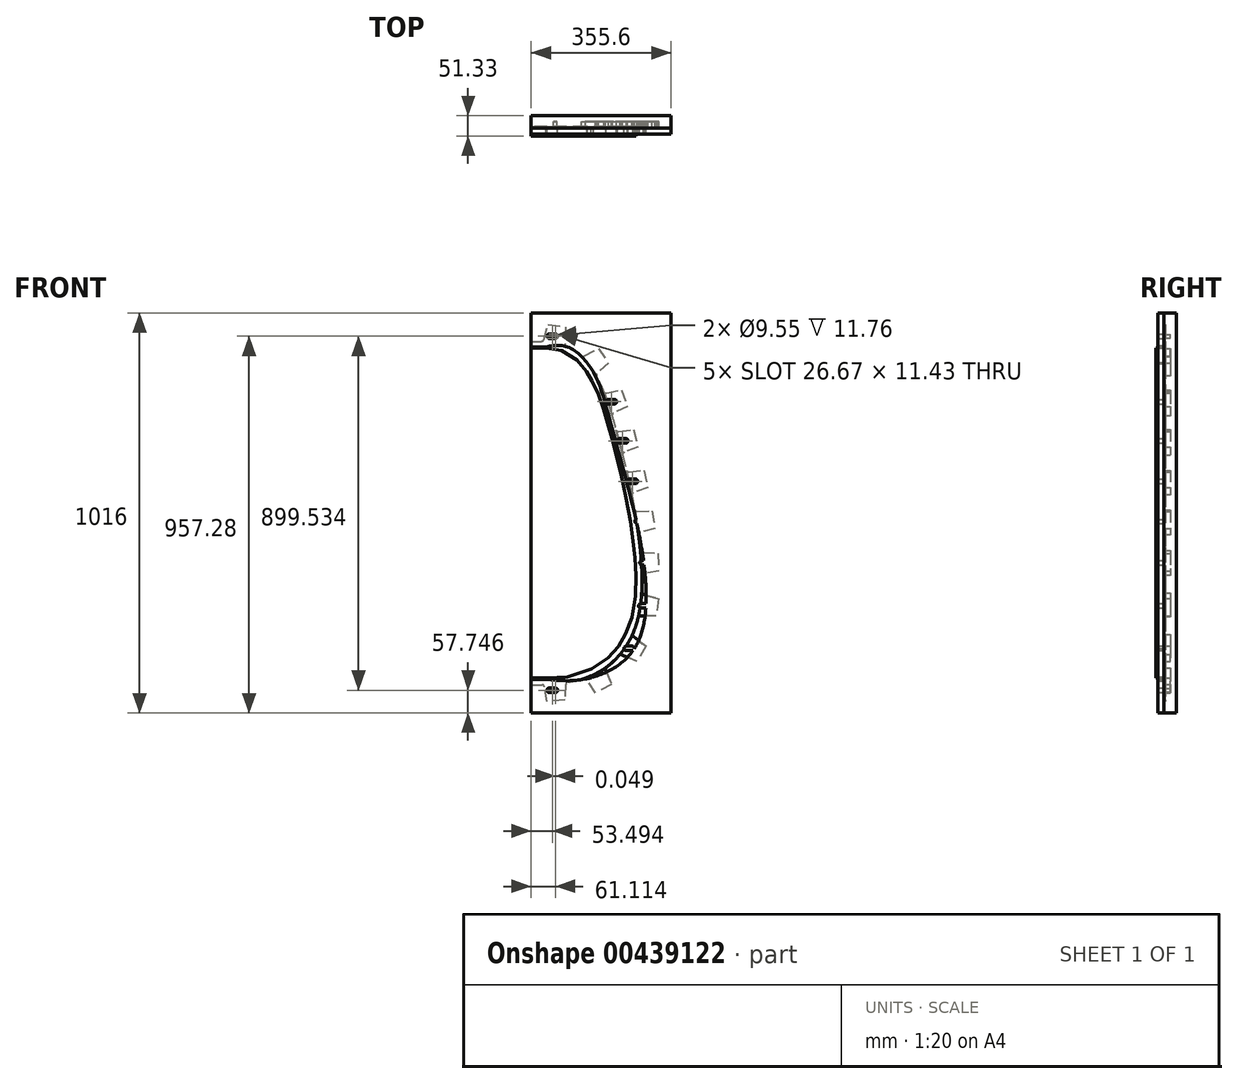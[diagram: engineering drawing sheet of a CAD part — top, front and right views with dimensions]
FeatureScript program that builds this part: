
annotation { "Feature Type Name" : "Feature", "Feature Type Description" : "" }
export const myFeature = defineFeature(function(context is Context, id is Id, definition is map)
    precondition{}
    {
        {
            var Q0;
            Q0=qCreatedBy(makeId("Front.planeOp"),FACE);
            var sketch = newSketch(context, id + "F0", { "sketchPlane" : qUnion([Q0])});
            skFitSpline(sketch, "E0", {"points": [v(-576.92, 670.47) * mm, v(-470.24, 606.97) * mm, v(-414.36, 467.27) * mm, v(-348.32, 137.07) * mm, v(-383.88, -82.64) * mm, v(-576.92, -174.08) * mm], "startDerivative": vector(1017.06, 0) * mm, "endDerivative": vector(-1410.71, 0) * mm});
            skLineSegment(sketch, "E1", {"start": v(-576.92, 670.47) * mm, "end": v(-576.92, -174.08) * mm, "construction": true});
            skFitSpline(sketch, "E2.MirrorCS", {"points": [v(-576.92, 670.47) * mm, v(-683.6, 606.97) * mm, v(-739.48, 467.27) * mm, v(-805.52, 137.07) * mm, v(-769.96, -82.64) * mm, v(-576.92, -174.08) * mm], "startDerivative": vector(-1017.06, 0) * mm, "endDerivative": vector(1410.71, 0) * mm});
            skSolve(sketch);
        }
        {
            var Q0;
            Q0=qCreatedBy(makeId("Front.planeOp"),FACE);
            var sketch = newSketch(context, id + "F1", { "sketchPlane" : qUnion([Q0])});
            skLineSegment(sketch, "E3.left", {"start": v(1043.34, 841.74) * mm, "end": v(1043.34, -174.26) * mm, "construction": true});
            skFitSpline(sketch, "E4", {"points": [v(1043.34, 756.01) * mm, v(1150.02, 692.51) * mm, v(1205.9, 552.81) * mm, v(1271.94, 222.61) * mm, v(1236.38, 2.9) * mm, v(1043.34, -88.54) * mm], "startDerivative": vector(1017.06, 0) * mm, "endDerivative": vector(-1775.42, 0) * mm});
            skFitSpline(sketch, "E5.0", {"points": [v(1043.34, 806.81) * mm, v(1050.54, 806.81) * mm, v(1064.65, 806) * mm, v(1084.8, 802.4) * mm, v(1103.69, 796.55) * mm, v(1121.1, 788.71) * mm, v(1136.85, 779.25) * mm, v(1150.91, 768.58) * mm, v(1161.28, 758.99) * mm, v(1168.83, 751.07) * mm, v(1174.15, 745.04) * mm, v(1179.14, 738.95) * mm, v(1183.83, 732.83) * mm, v(1187.5, 727.73) * mm, v(1190.31, 723.65) * mm, v(1192.36, 720.61) * mm, v(1194.35, 717.57) * mm, v(1196.96, 713.48) * mm, v(1200.11, 708.33) * mm, v(1203.75, 702.08) * mm, v(1208.4, 693.67) * mm, v(1213.85, 682.98) * mm, v(1219.89, 669.89) * mm, v(1225.5, 656.5) * mm, v(1232.5, 638.2) * mm, v(1238.98, 619.16) * mm, v(1244.47, 601.6) * mm, v(1247.59, 591.29) * mm, v(1249.93, 583.4) * mm, v(1251.9, 576.67) * mm, v(1253.47, 571.21) * mm, v(1254.66, 567.07) * mm, v(1255.86, 562.88) * mm, v(1257.48, 557.22) * mm, v(1259.52, 550) * mm, v(1262, 541.12) * mm, v(1265.36, 529) * mm, v(1269.6, 513.4) * mm, v(1274.72, 493.98) * mm, v(1281.54, 467.29) * mm, v(1289.92, 432.61) * mm, v(1299.39, 389.54) * mm, v(1307.88, 345.63) * mm, v(1313.83, 308.82) * mm, v(1317.72, 279.53) * mm, v(1320.15, 257.7) * mm, v(1321.73, 239.7) * mm, v(1322.7, 225.41) * mm, v(1323.45, 211.24) * mm, v(1324, 193.8) * mm, v(1324.03, 166.44) * mm, v(1322.49, 133.31) * mm, v(1318.05, 95.33) * mm, v(1312.15, 65.2) * mm, v(1306.08, 42.08) * mm, v(1301.7, 28.04) * mm, v(1297.85, 17.07) * mm, v(1294.78, 8.97) * mm, v(1291.54, 1) * mm, v(1288.68, -5.52) * mm, v(1286.3, -10.67) * mm, v(1284.48, -14.5) * mm, v(1282.6, -18.29) * mm, v(1280.69, -22.04) * mm, v(1278.7, -25.8) * mm, v(1275.96, -30.78) * mm, v(1272.35, -37) * mm, v(1267.69, -44.42) * mm, v(1260.99, -54.21) * mm, v(1251.62, -66.2) * mm, v(1238.62, -79.86) * mm, v(1223.79, -92.5) * mm, v(1207.15, -103.81) * mm, v(1188.83, -113.58) * mm, v(1168.9, -121.74) * mm, v(1147.4, -128.28) * mm, v(1124.3, -133.28) * mm, v(1099.43, -136.79) * mm, v(1072.64, -138.87) * mm, v(1053.37, -139.34) * mm, v(1043.34, -139.34) * mm]});
            skLineSegment(sketch, "E6", {"start": v(1043.34, 806.81) * mm, "end": v(1005.24, 806.81) * mm});
            skLineSegment(sketch, "E7", {"start": v(1005.24, 806.81) * mm, "end": v(1005.24, 756.01) * mm});
            skLineSegment(sketch, "E8", {"start": v(1005.24, 756.01) * mm, "end": v(1043.34, 756.01) * mm});
            skLineSegment(sketch, "E9", {"start": v(1043.34, -88.54) * mm, "end": v(1005.24, -88.54) * mm});
            skLineSegment(sketch, "E10", {"start": v(1005.24, -139.34) * mm, "end": v(1043.34, -139.34) * mm});
            skFitSpline(sketch, "E11.0", {"points": [v(1043.34, 784.67) * mm, v(1049.71, 784.67) * mm, v(1062.1, 783.95) * mm, v(1079.57, 780.82) * mm, v(1095.84, 775.78) * mm, v(1110.8, 769.04) * mm, v(1124.4, 760.88) * mm, v(1136.64, 751.6) * mm, v(1147.6, 741.46) * mm, v(1155.76, 732.53) * mm, v(1161.77, 725.2) * mm, v(1166.04, 719.62) * mm, v(1169.41, 714.95) * mm, v(1172, 711.19) * mm, v(1173.9, 708.37) * mm, v(1175.74, 705.55) * mm, v(1178.16, 701.75) * mm, v(1181.1, 696.97) * mm, v(1184.47, 691.16) * mm, v(1188.8, 683.32) * mm, v(1193.9, 673.32) * mm, v(1199.6, 660.98) * mm, v(1204.93, 648.27) * mm, v(1211.64, 630.76) * mm, v(1217.92, 612.3) * mm, v(1224.06, 592.64) * mm, v(1227.9, 579.8) * mm, v(1231.01, 569.16) * mm, v(1233.37, 560.99) * mm, v(1235.77, 552.6) * mm, v(1239.02, 541.12) * mm, v(1243.15, 526.26) * mm, v(1248.2, 507.67) * mm, v(1253.28, 488.41) * mm, v(1260.04, 461.96) * mm, v(1268.34, 427.62) * mm, v(1277.7, 385.05) * mm, v(1286.07, 341.74) * mm, v(1291.92, 305.55) * mm, v(1295.74, 276.84) * mm, v(1298.11, 255.5) * mm, v(1299.65, 237.95) * mm, v(1300.58, 224.07) * mm, v(1301.32, 210.33) * mm, v(1301.85, 193.43) * mm, v(1301.88, 166.98) * mm, v(1300.39, 135.07) * mm, v(1296.14, 98.7) * mm, v(1290.52, 70.05) * mm, v(1284.78, 48.18) * mm, v(1279.83, 32.3) * mm, v(1275.18, 19.55) * mm, v(1271.13, 9.62) * mm, v(1267.94, 2.32) * mm, v(1265.14, -3.64) * mm, v(1262.82, -8.34) * mm, v(1260.44, -12.98) * mm, v(1257.34, -18.74) * mm, v(1253.39, -25.56) * mm, v(1249.16, -32.28) * mm, v(1243.14, -41.07) * mm, v(1234.81, -51.72) * mm, v(1223.36, -63.75) * mm, v(1210.35, -74.85) * mm, v(1195.7, -84.8) * mm, v(1179.44, -93.48) * mm, v(1161.52, -100.82) * mm, v(1141.89, -106.8) * mm, v(1120.46, -111.44) * mm, v(1089.28, -115.85) * mm, v(1062.72, -117.19) * mm, v(1043.34, -117.19) * mm], "construction": true});
            skLineSegment(sketch, "E12", {"start": v(1043.34, -117.19) * mm, "end": v(1071.42, -116.5) * mm, "construction": true});
            skLineSegment(sketch, "E13", {"start": v(1071.42, -116.5) * mm, "end": v(1179.77, -92.97) * mm, "construction": true});
            skLineSegment(sketch, "E14", {"start": v(1179.77, -92.97) * mm, "end": v(1263.07, -7.82) * mm, "construction": true});
            skLineSegment(sketch, "E15", {"start": v(1263.07, -7.82) * mm, "end": v(1295.52, 97.75) * mm, "construction": true});
            skLineSegment(sketch, "E16", {"start": v(1295.52, 97.75) * mm, "end": v(1301.39, 207.04) * mm, "construction": true});
            skLineSegment(sketch, "E17", {"start": v(1301.39, 207.04) * mm, "end": v(1290.66, 312.82) * mm, "construction": true});
            skLineSegment(sketch, "E18", {"start": v(1290.66, 312.82) * mm, "end": v(1270.69, 416.63) * mm, "construction": true});
            skLineSegment(sketch, "E19", {"start": v(1270.69, 416.63) * mm, "end": v(1245.88, 516.18) * mm, "construction": true});
            skLineSegment(sketch, "E20", {"start": v(1245.88, 516.18) * mm, "end": v(1216.32, 616.8) * mm, "construction": true});
            skLineSegment(sketch, "E21", {"start": v(1216.32, 616.8) * mm, "end": v(1168.66, 715.98) * mm, "construction": true});
            skLineSegment(sketch, "E22", {"start": v(1168.66, 715.98) * mm, "end": v(1071.32, 782.2) * mm, "construction": true});
            skLineSegment(sketch, "E23", {"start": v(1071.32, 782.2) * mm, "end": v(1043.34, 784.67) * mm, "construction": true});
            skCircle(sketch, "E24", {"center": v(1071.42, -116.5) * mm, "radius": 4.76 * mm});
            skCircle(sketch, "E25", {"center": v(1179.77, -92.97) * mm, "radius": 4.76 * mm});
            skCircle(sketch, "E26", {"center": v(1263.07, -7.82) * mm, "radius": 4.76 * mm});
            skCircle(sketch, "E27", {"center": v(1295.52, 97.75) * mm, "radius": 4.76 * mm});
            skCircle(sketch, "E28", {"center": v(1301.39, 207.04) * mm, "radius": 4.76 * mm});
            skCircle(sketch, "E29", {"center": v(1290.66, 312.82) * mm, "radius": 4.76 * mm});
            skCircle(sketch, "E30", {"center": v(1270.69, 416.63) * mm, "radius": 4.76 * mm});
            skCircle(sketch, "E31", {"center": v(1245.88, 516.18) * mm, "radius": 4.76 * mm});
            skCircle(sketch, "E32", {"center": v(1216.32, 616.8) * mm, "radius": 4.76 * mm});
            skCircle(sketch, "E33", {"center": v(1168.66, 715.98) * mm, "radius": 4.76 * mm});
            skCircle(sketch, "E34", {"center": v(1071.32, 782.2) * mm, "radius": 4.76 * mm});
            skFitSpline(sketch, "E35.0", {"points": [v(1043.34, 752.4) * mm, v(1053.67, 752.4) * mm, v(1072.54, 750.1) * mm, v(1096.28, 740.96) * mm, v(1116.25, 727.3) * mm, v(1130.27, 713.02) * mm, v(1140.2, 700.45) * mm, v(1147.09, 690.59) * mm, v(1153.46, 680.47) * mm, v(1159.36, 670.04) * mm, v(1164.87, 659.25) * mm, v(1171.78, 644.27) * mm, v(1178.16, 628.3) * mm, v(1184.25, 611.1) * mm, v(1188.74, 597.54) * mm, v(1193.2, 583.23) * mm, v(1197.72, 568.14) * mm, v(1202.34, 552.2) * mm, v(1207.14, 535.36) * mm, v(1212.05, 517.7) * mm, v(1217.04, 499.33) * mm, v(1222.06, 480.3) * mm, v(1228.73, 454.2) * mm, v(1236.9, 420.35) * mm, v(1246.1, 378.5) * mm, v(1254.31, 336.06) * mm, v(1260.02, 300.77) * mm, v(1263.71, 272.91) * mm, v(1266.01, 252.3) * mm, v(1267.78, 232.03) * mm, v(1268.98, 212.22) * mm, v(1269.6, 192.89) * mm, v(1269.62, 167.77) * mm, v(1268.2, 137.64) * mm, v(1264.22, 103.61) * mm, v(1259.02, 77.1) * mm, v(1253.75, 57.06) * mm, v(1249.25, 42.62) * mm, v(1244.2, 28.78) * mm, v(1239.55, 17.76) * mm, v(1235.56, 9.26) * mm, v(1231.4, 0.97) * mm, v(1225.85, -8.98) * mm, v(1218.51, -20.19) * mm, v(1210.33, -30.64) * mm, v(1201.14, -40.3) * mm, v(1187.31, -52.07) * mm, v(1166.63, -64.67) * mm, v(1134.9, -76.05) * mm, v(1094.85, -83.24) * mm, v(1061.73, -84.93) * mm, v(1043.34, -84.93) * mm]});
            skLineSegment(sketch, "E36", {"start": v(1043.34, 752.4) * mm, "end": v(1005.24, 752.4) * mm});
            skLineSegment(sketch, "E37", {"start": v(1005.24, 756.01) * mm, "end": v(1005.24, 752.4) * mm});
            skLineSegment(sketch, "E38", {"start": v(1043.34, -117.19) * mm, "end": v(1005.24, -117.19) * mm});
            skLineSegment(sketch, "E39", {"start": v(1043.34, -84.93) * mm, "end": v(1005.24, -84.93) * mm});
            skLineSegment(sketch, "E40", {"start": v(1005.24, -139.34) * mm, "end": v(1005.24, -117.19) * mm});
            skLineSegment(sketch, "E41", {"start": v(1005.24, -88.54) * mm, "end": v(1005.24, -117.19) * mm});
            skLineSegment(sketch, "E42", {"start": v(1005.24, -88.54) * mm, "end": v(1005.24, -84.93) * mm});
            skLineSegment(sketch, "E43", {"start": v(1005.24, -84.93) * mm, "end": v(1005.24, 752.4) * mm});
            skFitSpline(sketch, "E44.0", {"points": [v(1043.34, 805.54) * mm, v(1050.5, 805.54) * mm, v(1064.5, 804.74) * mm, v(1084.5, 801.17) * mm, v(1103.24, 795.36) * mm, v(1120.5, 787.59) * mm, v(1136.14, 778.2) * mm, v(1150.1, 767.6) * mm, v(1160.4, 758.08) * mm, v(1167.9, 750.21) * mm, v(1173.18, 744.21) * mm, v(1178.15, 738.16) * mm, v(1182.8, 732.07) * mm, v(1186.47, 727) * mm, v(1189.26, 722.94) * mm, v(1191.3, 719.9) * mm, v(1193.28, 716.88) * mm, v(1195.88, 712.8) * mm, v(1199.02, 707.68) * mm, v(1202.64, 701.46) * mm, v(1207.27, 693.07) * mm, v(1212.7, 682.43) * mm, v(1218.72, 669.38) * mm, v(1224.32, 656.02) * mm, v(1231.31, 637.78) * mm, v(1237.78, 618.76) * mm, v(1243.25, 601.23) * mm, v(1246.37, 590.92) * mm, v(1248.71, 583.03) * mm, v(1250.67, 576.32) * mm, v(1252.25, 570.86) * mm, v(1253.44, 566.72) * mm, v(1254.64, 562.53) * mm, v(1256.26, 556.87) * mm, v(1258.3, 549.65) * mm, v(1260.78, 540.78) * mm, v(1264.13, 528.67) * mm, v(1268.37, 513.07) * mm, v(1273.49, 493.66) * mm, v(1280.3, 466.98) * mm, v(1288.68, 432.33) * mm, v(1298.14, 389.29) * mm, v(1306.63, 345.4) * mm, v(1312.57, 308.64) * mm, v(1316.46, 279.38) * mm, v(1318.89, 257.58) * mm, v(1320.46, 239.6) * mm, v(1321.43, 225.33) * mm, v(1322.18, 211.2) * mm, v(1322.73, 193.78) * mm, v(1322.76, 166.47) * mm, v(1321.22, 133.41) * mm, v(1316.8, 95.52) * mm, v(1310.91, 65.48) * mm, v(1304.85, 42.43) * mm, v(1300.5, 28.44) * mm, v(1296.66, 17.5) * mm, v(1293.6, 9.43) * mm, v(1290.37, 1.5) * mm, v(1287.52, -5) * mm, v(1285.16, -10.13) * mm, v(1283.34, -13.94) * mm, v(1281.47, -17.72) * mm, v(1279.56, -21.46) * mm, v(1277.58, -25.19) * mm, v(1274.86, -30.16) * mm, v(1271.27, -36.35) * mm, v(1266.63, -43.73) * mm, v(1259.96, -53.46) * mm, v(1250.66, -65.36) * mm, v(1237.75, -78.94) * mm, v(1223.02, -91.5) * mm, v(1206.5, -102.72) * mm, v(1188.29, -112.43) * mm, v(1168.48, -120.54) * mm, v(1147.09, -127.05) * mm, v(1124.07, -132.02) * mm, v(1099.3, -135.53) * mm, v(1072.58, -137.6) * mm, v(1053.35, -138.07) * mm, v(1043.34, -138.07) * mm], "construction": true});
            skFitSpline(sketch, "E45.0", {"points": [v(1043.34, 759.44) * mm, v(1054.2, 759.44) * mm, v(1074.2, 757) * mm, v(1099.6, 747.24) * mm, v(1120.84, 732.68) * mm, v(1135.55, 717.7) * mm, v(1145.87, 704.64) * mm, v(1152.96, 694.47) * mm, v(1159.5, 684.08) * mm, v(1167.58, 669.8) * mm, v(1176.64, 651.08) * mm, v(1184.75, 630.78) * mm, v(1190.9, 613.38) * mm, v(1195.44, 599.68) * mm, v(1199.94, 585.29) * mm, v(1204.47, 570.12) * mm, v(1209.1, 554.14) * mm, v(1213.9, 537.26) * mm, v(1218.83, 519.57) * mm, v(1223.84, 501.15) * mm, v(1228.87, 482.07) * mm, v(1235.56, 455.89) * mm, v(1243.77, 421.94) * mm, v(1253, 379.93) * mm, v(1261.24, 337.3) * mm, v(1266.97, 301.81) * mm, v(1270.7, 273.77) * mm, v(1273.01, 253) * mm, v(1274.8, 232.56) * mm, v(1276.01, 212.54) * mm, v(1276.63, 193) * mm, v(1276.66, 167.6) * mm, v(1275.23, 137.08) * mm, v(1271.18, 102.54) * mm, v(1265.9, 75.57) * mm, v(1260.52, 55.12) * mm, v(1255.92, 40.37) * mm, v(1250.76, 26.2) * mm, v(1245.99, 14.91) * mm, v(1241.89, 6.19) * mm, v(1237.6, -2.33) * mm, v(1231.89, -12.6) * mm, v(1224.25, -24.28) * mm, v(1212.81, -38.89) * mm, v(1195.75, -55.2) * mm, v(1169.6, -71.1) * mm, v(1136.62, -82.9) * mm, v(1095.57, -90.25) * mm, v(1061.94, -91.96) * mm, v(1043.34, -91.96) * mm], "construction": true});
            skFitSpline(sketch, "E46.0", {"points": [v(1043.34, 771.5) * mm, v(1049.22, 771.5) * mm, v(1060.58, 770.85) * mm, v(1076.47, 768) * mm, v(1091.18, 763.44) * mm, v(1104.69, 757.36) * mm, v(1117, 749.97) * mm, v(1128.16, 741.5) * mm, v(1138.25, 732.2) * mm, v(1145.83, 723.9) * mm, v(1151.46, 717.02) * mm, v(1155.48, 711.78) * mm, v(1159.3, 706.47) * mm, v(1162.34, 702) * mm, v(1164.7, 698.4) * mm, v(1167, 694.79) * mm, v(1169.8, 690.22) * mm, v(1173.03, 684.67) * mm, v(1177.17, 677.17) * mm, v(1182.07, 667.58) * mm, v(1189.38, 651.73) * mm, v(1197.7, 630.86) * mm, v(1205.41, 608.22) * mm, v(1211.48, 588.8) * mm, v(1215.29, 576.07) * mm, v(1218.38, 565.5) * mm, v(1220.72, 557.36) * mm, v(1223.11, 549) * mm, v(1226.35, 537.57) * mm, v(1230.47, 522.77) * mm, v(1235.5, 504.27) * mm, v(1240.55, 485.1) * mm, v(1247.27, 458.79) * mm, v(1255.52, 424.66) * mm, v(1264.81, 382.38) * mm, v(1273.12, 339.42) * mm, v(1280.07, 296.43) * mm, v(1284.41, 261.1) * mm, v(1286.53, 236.91) * mm, v(1287.45, 223.28) * mm, v(1288.17, 209.79) * mm, v(1288.7, 193.2) * mm, v(1288.72, 167.3) * mm, v(1287.26, 136.12) * mm, v(1283.12, 100.7) * mm, v(1277.67, 72.93) * mm, v(1272.12, 51.8) * mm, v(1267.36, 36.51) * mm, v(1262.89, 24.25) * mm, v(1259.01, 14.74) * mm, v(1255.95, 7.75) * mm, v(1253.28, 2.05) * mm, v(1251.06, -2.43) * mm, v(1248.8, -6.86) * mm, v(1245.85, -12.32) * mm, v(1240.88, -20.9) * mm, v(1234.08, -31.3) * mm, v(1224.83, -43.12) * mm, v(1214.3, -54.19) * mm, v(1202.36, -64.36) * mm, v(1188.9, -73.5) * mm, v(1173.86, -81.54) * mm, v(1157.13, -88.4) * mm, v(1138.61, -94.05) * mm, v(1118.18, -98.47) * mm, v(1088.17, -102.72) * mm, v(1062.31, -104.03) * mm, v(1043.34, -104.03) * mm], "construction": true});
            skLineSegment(sketch, "E47.bottom", {"start": v(1005.24, 841.74) * mm, "end": v(1360.84, 841.74) * mm});
            skLineSegment(sketch, "E47.top", {"start": v(1005.24, -174.26) * mm, "end": v(1360.84, -174.26) * mm});
            skLineSegment(sketch, "E47.right", {"start": v(1360.84, 841.74) * mm, "end": v(1360.84, -174.26) * mm});
            skLineSegment(sketch, "E48", {"start": v(1043.34, 771.5) * mm, "end": v(1015.4, 771.5) * mm, "construction": true});
            skLineSegment(sketch, "E49", {"start": v(1015.4, 771.5) * mm, "end": v(1015.4, 752.4) * mm, "construction": true});
            skLineSegment(sketch, "E50", {"start": v(1043.34, -104.03) * mm, "end": v(1015.4, -104.03) * mm});
            skLineSegment(sketch, "E51", {"start": v(1015.4, -104.03) * mm, "end": v(1015.4, -84.93) * mm});
            skLineSegment(sketch, "E52", {"start": v(1005.24, 841.74) * mm, "end": v(1005.24, 806.81) * mm});
            skLineSegment(sketch, "E53", {"start": v(1005.24, -174.26) * mm, "end": v(1005.24, -139.34) * mm});
            skLineSegment(sketch, "E54.bottom", {"start": v(-615.02, 756.2) * mm, "end": v(-259.42, 756.2) * mm});
            skLineSegment(sketch, "E54.top", {"start": v(-615.02, -259.8) * mm, "end": v(-259.42, -259.8) * mm});
            skLineSegment(sketch, "E54.left", {"start": v(-615.02, 756.2) * mm, "end": v(-615.02, -259.8) * mm});
            skLineSegment(sketch, "E54.right", {"start": v(-259.42, 756.2) * mm, "end": v(-259.42, -259.8) * mm});
            skPoint(sketch, "E55", {"position": v(-615.02, 248.2) * mm});
            skSolve(sketch);
        }
        {
            var Q0;
            Q0=makeQuery(id+"F1.imprint","IMPRINT",FACE,{"disambiguationData":[TD([[makeQuery(id+"F1.imprint","IMPRINT",EDGE,{"derivedFrom":sQuery(id+"F1.wireOp",EDGE,"E54.bottom")}),-1.0]])]});
            extrude(context, id + "F2", {"entities" : qUnion([Q0]), "depth" : 15.32 * mm, "offsetDistance" : 25.4 * mm});
        }
        {
            var Q0;
            Q0=qCreatedBy(makeId("Front.planeOp"),FACE);
            var sketch = newSketch(context, id + "F3", { "sketchPlane" : qUnion([Q0])});
            skLineSegment(sketch, "E56", {"start": v(-576.92, -202.73) * mm, "end": v(-553.86, -202.05) * mm, "construction": true});
            skLineSegment(sketch, "E57", {"start": v(-553.86, -202.05) * mm, "end": v(-444.03, -174.3) * mm, "construction": true});
            skLineSegment(sketch, "E58", {"start": v(-444.03, -174.3) * mm, "end": v(-358.34, -95.84) * mm, "construction": true});
            skLineSegment(sketch, "E59", {"start": v(-358.34, -95.84) * mm, "end": v(-321.43, 12.15) * mm, "construction": true});
            skLineSegment(sketch, "E60", {"start": v(-321.43, 12.15) * mm, "end": v(-318.47, 121.78) * mm, "construction": true});
            skLineSegment(sketch, "E61", {"start": v(-318.47, 121.78) * mm, "end": v(-330.75, 227.4) * mm, "construction": true});
            skLineSegment(sketch, "E62", {"start": v(-330.75, 227.4) * mm, "end": v(-350.13, 328.81) * mm, "construction": true});
            skLineSegment(sketch, "E63", {"start": v(-350.13, 328.81) * mm, "end": v(-374.98, 431.7) * mm, "construction": true});
            skLineSegment(sketch, "E64", {"start": v(-374.98, 431.7) * mm, "end": v(-403.72, 531.13) * mm, "construction": true});
            skLineSegment(sketch, "E65", {"start": v(-403.72, 531.13) * mm, "end": v(-453.17, 632.57) * mm, "construction": true});
            skLineSegment(sketch, "E66", {"start": v(-453.17, 632.57) * mm, "end": v(-553.9, 697.48) * mm, "construction": true});
            skLineSegment(sketch, "E67", {"start": v(-553.9, 697.48) * mm, "end": v(-576.92, 699.12) * mm, "construction": true});
            skCircle(sketch, "E68", {"center": v(-553.9, 697.48) * mm, "radius": 5.23 * mm});
            skLineSegment(sketch, "E69", {"start": v(-579.9, 676.7) * mm, "end": v(-567.43, 720.37) * mm});
            skLineSegment(sketch, "E70", {"start": v(-567.43, 720.37) * mm, "end": v(-533.92, 715.02) * mm});
            skLineSegment(sketch, "E71", {"start": v(-533.92, 715.02) * mm, "end": v(-535.69, 669.42) * mm});
            skLineSegment(sketch, "E72", {"start": v(-550.68, 717.7) * mm, "end": v(-553.08, 702.65) * mm, "construction": true});
            skLineSegment(sketch, "E73", {"start": v(-580.98, 672.9) * mm, "end": v(-535.83, 665.68) * mm, "construction": true});
            skFitSpline(sketch, "E74.0", {"points": [v(-576.92, 670.47) * mm, v(-523.93, 670.47) * mm, v(-458.36, 608.09) * mm, v(-410.1, 464.42) * mm, v(-331.77, 140.23) * mm, v(-355.6, -100.03) * mm, v(-480.52, -174.08) * mm, v(-576.92, -174.08) * mm]});
            skFitSpline(sketch, "E75.0", {"points": [v(-576.92, 666.79) * mm, v(-566.6, 666.79) * mm, v(-547.75, 664.48) * mm, v(-524.04, 655.35) * mm, v(-504.1, 641.7) * mm, v(-490.08, 627.43) * mm, v(-480.14, 614.86) * mm, v(-474.39, 606.64) * mm, v(-470.04, 599.94) * mm, v(-465.85, 593.14) * mm, v(-460.9, 584.46) * mm, v(-455.36, 573.66) * mm, v(-448.4, 558.7) * mm, v(-442, 542.73) * mm, v(-435.9, 525.54) * mm, v(-431.43, 511.98) * mm, v(-427, 497.68) * mm, v(-422.53, 482.59) * mm, v(-418, 466.65) * mm, v(-413.31, 449.82) * mm, v(-408.54, 432.17) * mm, v(-403.7, 413.8) * mm, v(-398.84, 394.77) * mm, v(-392.38, 368.66) * mm, v(-384.44, 334.82) * mm, v(-375.44, 292.95) * mm, v(-367.28, 250.5) * mm, v(-361.43, 215.2) * mm, v(-357.47, 187.32) * mm, v(-354.9, 166.7) * mm, v(-352.77, 146.41) * mm, v(-351.12, 126.58) * mm, v(-349.98, 107.24) * mm, v(-349.19, 82.11) * mm, v(-349.64, 52) * mm, v(-352.74, 18) * mm, v(-358.65, -13.71) * mm, v(-366.12, -38.19) * mm, v(-373.74, -56.55) * mm, v(-380.32, -69.7) * mm, v(-387.78, -82.24) * mm, v(-396.16, -94.14) * mm, v(-405.48, -105.36) * mm, v(-419.19, -119.34) * mm, v(-438.78, -134.9) * mm, v(-466.42, -150.13) * mm, v(-509.04, -165.34) * mm, v(-547.81, -170.4) * mm, v(-576.92, -170.4) * mm]});
            skLineSegment(sketch, "E76", {"start": v(-576.92, 666.79) * mm, "end": v(-576.92, 670.47) * mm});
            skLineSegment(sketch, "E77", {"start": v(-576.92, -174.08) * mm, "end": v(-576.92, -170.4) * mm});
            skFitSpline(sketch, "E78.0", {"points": [v(-576.92, 699.12) * mm, v(-570.55, 699.12) * mm, v(-558.17, 698.4) * mm, v(-540.7, 695.28) * mm, v(-524.43, 690.24) * mm, v(-509.48, 683.5) * mm, v(-495.89, 675.34) * mm, v(-483.65, 666.05) * mm, v(-472.7, 655.92) * mm, v(-464.54, 647) * mm, v(-458.53, 639.67) * mm, v(-454.26, 634.1) * mm, v(-450.88, 629.43) * mm, v(-448.29, 625.68) * mm, v(-446.4, 622.87) * mm, v(-444.54, 620.05) * mm, v(-442.12, 616.26) * mm, v(-439.17, 611.48) * mm, v(-435.78, 605.68) * mm, v(-431.43, 597.84) * mm, v(-426.3, 587.84) * mm, v(-420.56, 575.5) * mm, v(-415.2, 562.77) * mm, v(-408.45, 545.23) * mm, v(-402.15, 526.73) * mm, v(-396.04, 507.03) * mm, v(-392.23, 494.15) * mm, v(-389.17, 483.49) * mm, v(-386.85, 475.3) * mm, v(-384.5, 466.89) * mm, v(-381.32, 455.4) * mm, v(-377.3, 440.51) * mm, v(-372.4, 421.91) * mm, v(-367.48, 402.66) * mm, v(-360.94, 376.21) * mm, v(-352.9, 341.92) * mm, v(-343.76, 299.42) * mm, v(-335.45, 256.23) * mm, v(-329.47, 220.17) * mm, v(-325.42, 191.6) * mm, v(-322.78, 170.39) * mm, v(-320.58, 149.46) * mm, v(-318.87, 128.9) * mm, v(-317.68, 108.72) * mm, v(-316.84, 82.35) * mm, v(-317.31, 50.4) * mm, v(-320.65, 13.7) * mm, v(-327.14, -21.28) * mm, v(-337.23, -54.43) * mm, v(-349, -80.33) * mm, v(-360.61, -99.84) * mm, v(-370.45, -113.8) * mm, v(-381.45, -127.04) * mm, v(-397.66, -143.59) * mm, v(-420.84, -162) * mm, v(-453.22, -179.8) * mm, v(-489.97, -192.88) * mm, v(-530.96, -200.9) * mm, v(-561.12, -202.73) * mm, v(-576.92, -202.73) * mm], "construction": true});
            skLineSegment(sketch, "E79", {"start": v(-553.08, 702.65) * mm, "end": v(-558.4, 669.29) * mm, "construction": true});
            skCircle(sketch, "E80", {"center": v(-453.17, 632.57) * mm, "radius": 5.23 * mm});
            skLineSegment(sketch, "E81", {"start": v(-486.17, 636.39) * mm, "end": v(-446.47, 658.3) * mm});
            skLineSegment(sketch, "E82", {"start": v(-446.47, 658.3) * mm, "end": v(-426.64, 630.77) * mm});
            skLineSegment(sketch, "E83", {"start": v(-426.64, 630.77) * mm, "end": v(-459.52, 600.52) * mm});
            skLineSegment(sketch, "E84", {"start": v(-436.55, 644.53) * mm, "end": v(-448.92, 635.63) * mm, "construction": true});
            skLineSegment(sketch, "E85", {"start": v(-489.7, 634.44) * mm, "end": v(-462.98, 597.34) * mm, "construction": true});
            skLineSegment(sketch, "E86", {"start": v(-448.92, 635.63) * mm, "end": v(-476.34, 615.9) * mm, "construction": true});
            skCircle(sketch, "E87", {"center": v(-403.72, 531.13) * mm, "radius": 5.23 * mm});
            skLineSegment(sketch, "E88", {"start": v(-433, 544.72) * mm, "end": v(-389.75, 553.76) * mm});
            skLineSegment(sketch, "E89", {"start": v(-389.75, 553.76) * mm, "end": v(-378.9, 521.6) * mm});
            skLineSegment(sketch, "E90", {"start": v(-378.9, 521.6) * mm, "end": v(-418.82, 502.55) * mm});
            skLineSegment(sketch, "E91", {"start": v(-384.32, 537.68) * mm, "end": v(-398.76, 532.8) * mm, "construction": true});
            skLineSegment(sketch, "E92", {"start": v(-438.08, 543.65) * mm, "end": v(-423.45, 500.34) * mm, "construction": true});
            skLineSegment(sketch, "E93", {"start": v(-398.76, 532.8) * mm, "end": v(-430.77, 522) * mm, "construction": true});
            skCircle(sketch, "E94", {"center": v(-374.98, 431.7) * mm, "radius": 5.23 * mm});
            skLineSegment(sketch, "E95", {"start": v(-403.07, 447.42) * mm, "end": v(-359.38, 453.23) * mm});
            skLineSegment(sketch, "E96", {"start": v(-359.38, 453.23) * mm, "end": v(-350.93, 420.37) * mm});
            skLineSegment(sketch, "E97", {"start": v(-350.93, 420.37) * mm, "end": v(-391.75, 404.46) * mm});
            skLineSegment(sketch, "E98", {"start": v(-355.15, 436.8) * mm, "end": v(-369.91, 433) * mm, "construction": true});
            skLineSegment(sketch, "E99", {"start": v(-408.33, 446.72) * mm, "end": v(-396.93, 402.44) * mm, "construction": true});
            skLineSegment(sketch, "E100", {"start": v(-369.91, 433) * mm, "end": v(-402.63, 424.58) * mm, "construction": true});
            skCircle(sketch, "E101", {"center": v(-350.13, 328.81) * mm, "radius": 5.23 * mm});
            skLineSegment(sketch, "E102", {"start": v(-377.5, 345.53) * mm, "end": v(-333.78, 349.79) * mm});
            skLineSegment(sketch, "E103", {"start": v(-333.78, 349.79) * mm, "end": v(-326.48, 316.65) * mm});
            skLineSegment(sketch, "E104", {"start": v(-326.48, 316.65) * mm, "end": v(-368.02, 302.12) * mm});
            skLineSegment(sketch, "E105", {"start": v(-330.13, 333.22) * mm, "end": v(-345.02, 329.94) * mm, "construction": true});
            skLineSegment(sketch, "E106", {"start": v(-382.92, 345) * mm, "end": v(-373.09, 300.35) * mm, "construction": true});
            skLineSegment(sketch, "E107", {"start": v(-345.02, 329.94) * mm, "end": v(-378, 322.67) * mm, "construction": true});
            skCircle(sketch, "E108", {"center": v(-330.75, 227.4) * mm, "radius": 5.23 * mm});
            skLineSegment(sketch, "E109", {"start": v(-357.21, 245.76) * mm, "end": v(-313.14, 247.32) * mm});
            skLineSegment(sketch, "E110", {"start": v(-313.14, 247.32) * mm, "end": v(-307.9, 213.8) * mm});
            skLineSegment(sketch, "E111", {"start": v(-307.9, 213.8) * mm, "end": v(-350.19, 201.88) * mm});
            skLineSegment(sketch, "E112", {"start": v(-310.52, 230.56) * mm, "end": v(-325.58, 228.2) * mm, "construction": true});
            skLineSegment(sketch, "E113", {"start": v(-362.48, 245.58) * mm, "end": v(-355.42, 200.4) * mm, "construction": true});
            skLineSegment(sketch, "E114", {"start": v(-325.58, 228.2) * mm, "end": v(-358.95, 223) * mm, "construction": true});
            skCircle(sketch, "E115", {"center": v(-318.47, 121.78) * mm, "radius": 5.23 * mm});
            skLineSegment(sketch, "E116", {"start": v(-343.2, 142.67) * mm, "end": v(-299, 139.88) * mm});
            skLineSegment(sketch, "E117", {"start": v(-299, 139.88) * mm, "end": v(-297.07, 106) * mm});
            skLineSegment(sketch, "E118", {"start": v(-297.07, 106) * mm, "end": v(-340.45, 98.28) * mm});
            skLineSegment(sketch, "E119", {"start": v(-298.04, 122.94) * mm, "end": v(-313.25, 122.08) * mm, "construction": true});
            skLineSegment(sketch, "E120", {"start": v(-348.27, 143) * mm, "end": v(-345.68, 97.35) * mm, "construction": true});
            skLineSegment(sketch, "E121", {"start": v(-313.25, 122.08) * mm, "end": v(-346.98, 120.17) * mm, "construction": true});
            skCircle(sketch, "E122", {"center": v(-321.43, 12.15) * mm, "radius": 5.23 * mm});
            skLineSegment(sketch, "E123", {"start": v(-341.79, 37.4) * mm, "end": v(-298.84, 26.18) * mm});
            skLineSegment(sketch, "E124", {"start": v(-298.84, 26.18) * mm, "end": v(-303.45, -7.44) * mm});
            skLineSegment(sketch, "E125", {"start": v(-303.45, -7.44) * mm, "end": v(-348.15, -6.7) * mm});
            skLineSegment(sketch, "E126", {"start": v(-301.15, 9.37) * mm, "end": v(-316.25, 11.44) * mm, "construction": true});
            skLineSegment(sketch, "E127", {"start": v(-346.61, 38.67) * mm, "end": v(-352.82, -6.63) * mm, "construction": true});
            skLineSegment(sketch, "E128", {"start": v(-316.25, 11.44) * mm, "end": v(-349.72, 16.02) * mm, "construction": true});
            skCircle(sketch, "E129", {"center": v(-358.34, -95.84) * mm, "radius": 5.23 * mm});
            skLineSegment(sketch, "E130", {"start": v(-367.4, -64.47) * mm, "end": v(-332.07, -91.76) * mm});
            skLineSegment(sketch, "E131", {"start": v(-332.07, -91.76) * mm, "end": v(-349.45, -120.9) * mm});
            skLineSegment(sketch, "E132", {"start": v(-349.45, -120.9) * mm, "end": v(-391.09, -102.4) * mm});
            skLineSegment(sketch, "E133", {"start": v(-340.76, -106.33) * mm, "end": v(-353.85, -98.52) * mm, "construction": true});
            skLineSegment(sketch, "E134", {"start": v(-371.15, -61.58) * mm, "end": v(-394.57, -100.85) * mm, "construction": true});
            skLineSegment(sketch, "E135", {"start": v(-353.85, -98.52) * mm, "end": v(-382.86, -81.22) * mm, "construction": true});
            skCircle(sketch, "E136", {"center": v(-444.03, -174.3) * mm, "radius": 5.23 * mm});
            skLineSegment(sketch, "E137", {"start": v(-435.51, -142.82) * mm, "end": v(-419.44, -184.41) * mm});
            skLineSegment(sketch, "E138", {"start": v(-419.44, -184.41) * mm, "end": v(-449.4, -200.34) * mm});
            skLineSegment(sketch, "E139", {"start": v(-449.4, -200.34) * mm, "end": v(-475.45, -162.93) * mm});
            skLineSegment(sketch, "E140", {"start": v(-434.42, -192.38) * mm, "end": v(-441.57, -178.92) * mm, "construction": true});
            skLineSegment(sketch, "E141", {"start": v(-437.24, -138.36) * mm, "end": v(-477.61, -159.82) * mm, "construction": true});
            skLineSegment(sketch, "E142", {"start": v(-441.57, -178.92) * mm, "end": v(-457.42, -149.09) * mm, "construction": true});
            skCircle(sketch, "E143", {"center": v(-553.86, -202.05) * mm, "radius": 5.23 * mm});
            skLineSegment(sketch, "E144", {"start": v(-533.23, -176.97) * mm, "end": v(-535.55, -221.33) * mm});
            skLineSegment(sketch, "E145", {"start": v(-535.55, -221.33) * mm, "end": v(-569.4, -223.62) * mm});
            skLineSegment(sketch, "E146", {"start": v(-569.4, -223.62) * mm, "end": v(-577.71, -179.75) * mm});
            skLineSegment(sketch, "E147", {"start": v(-552.48, -222.48) * mm, "end": v(-553.5, -207.27) * mm, "construction": true});
            skLineSegment(sketch, "E148", {"start": v(-532.98, -172.03) * mm, "end": v(-578.6, -175.11) * mm, "construction": true});
            skLineSegment(sketch, "E149", {"start": v(-553.5, -207.27) * mm, "end": v(-555.78, -173.57) * mm, "construction": true});
            skLineSegment(sketch, "E150", {"start": v(-576.92, -179.67) * mm, "end": v(-576.92, -174.08) * mm});
            skFitSpline(sketch, "E151.trimOffspring", {"points": [v(-576.92, 676.06) * mm, v(-565.9, 676.06) * mm, v(-550.64, 674.2) * mm, v(-532.6, 668.6) * mm, v(-520.2, 663.02) * mm, v(-508.86, 656.21) * mm, v(-498.52, 648.37) * mm, v(-489.1, 639.67) * mm, v(-480.52, 630.28) * mm, v(-473.99, 622.03) * mm, v(-469.1, 615.25) * mm, v(-465.58, 610.1) * mm, v(-462.2, 604.9) * mm, v(-457.87, 597.85) * mm, v(-452.75, 588.87) * mm, v(-447.02, 577.73) * mm, v(-439.88, 562.33) * mm, v(-433.33, 546) * mm, v(-427.13, 528.53) * mm, v(-422.6, 514.8) * mm, v(-418.12, 500.36) * mm, v(-413.63, 485.17) * mm, v(-409.07, 469.16) * mm, v(-404.37, 452.27) * mm, v(-399.58, 434.56) * mm, v(-394.72, 416.12) * mm, v(-389.84, 397.03) * mm, v(-383.36, 370.82) * mm, v(-375.4, 336.85) * mm, v(-366.36, 294.8) * mm, v(-358.15, 252.14) * mm, v(-352.26, 216.62) * mm, v(-348.28, 188.55) * mm, v(-345.7, 167.75) * mm, v(-343.54, 147.28) * mm, v(-341.87, 127.24) * mm, v(-340.72, 107.66) * mm, v(-339.92, 82.18) * mm, v(-340.37, 51.54) * mm, v(-343.54, 16.78) * mm, v(-349.61, -15.88) * mm, v(-357.35, -41.26) * mm, v(-365.3, -60.4) * mm, v(-372.17, -74.15) * mm, v(-379.99, -87.29) * mm, v(-388.79, -99.78) * mm, v(-398.59, -111.57) * mm, v(-413.02, -126.3) * mm, v(-433.64, -142.67) * mm, v(-462.63, -158.64) * mm, v(-495.97, -170.52) * mm, v(-533.76, -177.94) * mm, v(-562, -179.67) * mm, v(-576.92, -179.67) * mm]});
            skFitSpline(sketch, "E152.trimOffspring", {"points": [v(-576.92, 676.06) * mm, v(-565.9, 676.06) * mm, v(-550.64, 674.2) * mm, v(-532.6, 668.6) * mm, v(-520.2, 663.02) * mm, v(-508.86, 656.21) * mm, v(-498.52, 648.37) * mm, v(-489.1, 639.67) * mm, v(-480.52, 630.28) * mm, v(-473.99, 622.03) * mm, v(-469.1, 615.25) * mm, v(-465.58, 610.1) * mm, v(-462.2, 604.9) * mm, v(-457.87, 597.85) * mm, v(-452.75, 588.87) * mm, v(-447.02, 577.73) * mm, v(-439.88, 562.33) * mm, v(-433.33, 546) * mm, v(-427.13, 528.53) * mm, v(-422.6, 514.8) * mm, v(-418.12, 500.36) * mm, v(-413.63, 485.17) * mm, v(-409.07, 469.16) * mm, v(-404.37, 452.27) * mm, v(-399.58, 434.56) * mm, v(-394.72, 416.12) * mm, v(-389.84, 397.03) * mm, v(-383.36, 370.82) * mm, v(-375.4, 336.85) * mm, v(-366.36, 294.8) * mm, v(-358.15, 252.14) * mm, v(-352.26, 216.62) * mm, v(-348.28, 188.55) * mm, v(-345.7, 167.75) * mm, v(-343.54, 147.28) * mm, v(-341.87, 127.24) * mm, v(-340.72, 107.66) * mm, v(-339.92, 82.18) * mm, v(-340.37, 51.54) * mm, v(-343.54, 16.78) * mm, v(-349.61, -15.88) * mm, v(-357.35, -41.26) * mm, v(-365.3, -60.4) * mm, v(-372.17, -74.15) * mm, v(-379.99, -87.29) * mm, v(-388.79, -99.78) * mm, v(-398.59, -111.57) * mm, v(-413.02, -126.3) * mm, v(-433.64, -142.67) * mm, v(-462.63, -158.64) * mm, v(-495.97, -170.52) * mm, v(-533.76, -177.94) * mm, v(-562, -179.67) * mm, v(-576.92, -179.67) * mm]});
            skFitSpline(sketch, "E153.trimOffspring", {"points": [v(-576.92, 676.06) * mm, v(-565.9, 676.06) * mm, v(-550.64, 674.2) * mm, v(-532.6, 668.6) * mm, v(-520.2, 663.02) * mm, v(-508.86, 656.21) * mm, v(-498.52, 648.37) * mm, v(-489.1, 639.67) * mm, v(-480.52, 630.28) * mm, v(-473.99, 622.03) * mm, v(-469.1, 615.25) * mm, v(-465.58, 610.1) * mm, v(-462.2, 604.9) * mm, v(-457.87, 597.85) * mm, v(-452.75, 588.87) * mm, v(-447.02, 577.73) * mm, v(-439.88, 562.33) * mm, v(-433.33, 546) * mm, v(-427.13, 528.53) * mm, v(-422.6, 514.8) * mm, v(-418.12, 500.36) * mm, v(-413.63, 485.17) * mm, v(-409.07, 469.16) * mm, v(-404.37, 452.27) * mm, v(-399.58, 434.56) * mm, v(-394.72, 416.12) * mm, v(-389.84, 397.03) * mm, v(-383.36, 370.82) * mm, v(-375.4, 336.85) * mm, v(-366.36, 294.8) * mm, v(-358.15, 252.14) * mm, v(-352.26, 216.62) * mm, v(-348.28, 188.55) * mm, v(-345.7, 167.75) * mm, v(-343.54, 147.28) * mm, v(-341.87, 127.24) * mm, v(-340.72, 107.66) * mm, v(-339.92, 82.18) * mm, v(-340.37, 51.54) * mm, v(-343.54, 16.78) * mm, v(-349.61, -15.88) * mm, v(-357.35, -41.26) * mm, v(-365.3, -60.4) * mm, v(-372.17, -74.15) * mm, v(-379.99, -87.29) * mm, v(-388.79, -99.78) * mm, v(-398.59, -111.57) * mm, v(-413.02, -126.3) * mm, v(-433.64, -142.67) * mm, v(-462.63, -158.64) * mm, v(-495.97, -170.52) * mm, v(-533.76, -177.94) * mm, v(-562, -179.67) * mm, v(-576.92, -179.67) * mm]});
            skFitSpline(sketch, "E154.trimOffspring", {"points": [v(-576.92, 676.06) * mm, v(-565.9, 676.06) * mm, v(-550.64, 674.2) * mm, v(-532.6, 668.6) * mm, v(-520.2, 663.02) * mm, v(-508.86, 656.21) * mm, v(-498.52, 648.37) * mm, v(-489.1, 639.67) * mm, v(-480.52, 630.28) * mm, v(-473.99, 622.03) * mm, v(-469.1, 615.25) * mm, v(-465.58, 610.1) * mm, v(-462.2, 604.9) * mm, v(-457.87, 597.85) * mm, v(-452.75, 588.87) * mm, v(-447.02, 577.73) * mm, v(-439.88, 562.33) * mm, v(-433.33, 546) * mm, v(-427.13, 528.53) * mm, v(-422.6, 514.8) * mm, v(-418.12, 500.36) * mm, v(-413.63, 485.17) * mm, v(-409.07, 469.16) * mm, v(-404.37, 452.27) * mm, v(-399.58, 434.56) * mm, v(-394.72, 416.12) * mm, v(-389.84, 397.03) * mm, v(-383.36, 370.82) * mm, v(-375.4, 336.85) * mm, v(-366.36, 294.8) * mm, v(-358.15, 252.14) * mm, v(-352.26, 216.62) * mm, v(-348.28, 188.55) * mm, v(-345.7, 167.75) * mm, v(-343.54, 147.28) * mm, v(-341.87, 127.24) * mm, v(-340.72, 107.66) * mm, v(-339.92, 82.18) * mm, v(-340.37, 51.54) * mm, v(-343.54, 16.78) * mm, v(-349.61, -15.88) * mm, v(-357.35, -41.26) * mm, v(-365.3, -60.4) * mm, v(-372.17, -74.15) * mm, v(-379.99, -87.29) * mm, v(-388.79, -99.78) * mm, v(-398.59, -111.57) * mm, v(-413.02, -126.3) * mm, v(-433.64, -142.67) * mm, v(-462.63, -158.64) * mm, v(-495.97, -170.52) * mm, v(-533.76, -177.94) * mm, v(-562, -179.67) * mm, v(-576.92, -179.67) * mm]});
            skFitSpline(sketch, "E155.trimOffspring", {"points": [v(-576.92, 676.06) * mm, v(-565.9, 676.06) * mm, v(-550.64, 674.2) * mm, v(-532.6, 668.6) * mm, v(-520.2, 663.02) * mm, v(-508.86, 656.21) * mm, v(-498.52, 648.37) * mm, v(-489.1, 639.67) * mm, v(-480.52, 630.28) * mm, v(-473.99, 622.03) * mm, v(-469.1, 615.25) * mm, v(-465.58, 610.1) * mm, v(-462.2, 604.9) * mm, v(-457.87, 597.85) * mm, v(-452.75, 588.87) * mm, v(-447.02, 577.73) * mm, v(-439.88, 562.33) * mm, v(-433.33, 546) * mm, v(-427.13, 528.53) * mm, v(-422.6, 514.8) * mm, v(-418.12, 500.36) * mm, v(-413.63, 485.17) * mm, v(-409.07, 469.16) * mm, v(-404.37, 452.27) * mm, v(-399.58, 434.56) * mm, v(-394.72, 416.12) * mm, v(-389.84, 397.03) * mm, v(-383.36, 370.82) * mm, v(-375.4, 336.85) * mm, v(-366.36, 294.8) * mm, v(-358.15, 252.14) * mm, v(-352.26, 216.62) * mm, v(-348.28, 188.55) * mm, v(-345.7, 167.75) * mm, v(-343.54, 147.28) * mm, v(-341.87, 127.24) * mm, v(-340.72, 107.66) * mm, v(-339.92, 82.18) * mm, v(-340.37, 51.54) * mm, v(-343.54, 16.78) * mm, v(-349.61, -15.88) * mm, v(-357.35, -41.26) * mm, v(-365.3, -60.4) * mm, v(-372.17, -74.15) * mm, v(-379.99, -87.29) * mm, v(-388.79, -99.78) * mm, v(-398.59, -111.57) * mm, v(-413.02, -126.3) * mm, v(-433.64, -142.67) * mm, v(-462.63, -158.64) * mm, v(-495.97, -170.52) * mm, v(-533.76, -177.94) * mm, v(-562, -179.67) * mm, v(-576.92, -179.67) * mm]});
            skFitSpline(sketch, "E156.trimOffspring", {"points": [v(-576.92, 676.06) * mm, v(-565.9, 676.06) * mm, v(-550.64, 674.2) * mm, v(-532.6, 668.6) * mm, v(-520.2, 663.02) * mm, v(-508.86, 656.21) * mm, v(-498.52, 648.37) * mm, v(-489.1, 639.67) * mm, v(-480.52, 630.28) * mm, v(-473.99, 622.03) * mm, v(-469.1, 615.25) * mm, v(-465.58, 610.1) * mm, v(-462.2, 604.9) * mm, v(-457.87, 597.85) * mm, v(-452.75, 588.87) * mm, v(-447.02, 577.73) * mm, v(-439.88, 562.33) * mm, v(-433.33, 546) * mm, v(-427.13, 528.53) * mm, v(-422.6, 514.8) * mm, v(-418.12, 500.36) * mm, v(-413.63, 485.17) * mm, v(-409.07, 469.16) * mm, v(-404.37, 452.27) * mm, v(-399.58, 434.56) * mm, v(-394.72, 416.12) * mm, v(-389.84, 397.03) * mm, v(-383.36, 370.82) * mm, v(-375.4, 336.85) * mm, v(-366.36, 294.8) * mm, v(-358.15, 252.14) * mm, v(-352.26, 216.62) * mm, v(-348.28, 188.55) * mm, v(-345.7, 167.75) * mm, v(-343.54, 147.28) * mm, v(-341.87, 127.24) * mm, v(-340.72, 107.66) * mm, v(-339.92, 82.18) * mm, v(-340.37, 51.54) * mm, v(-343.54, 16.78) * mm, v(-349.61, -15.88) * mm, v(-357.35, -41.26) * mm, v(-365.3, -60.4) * mm, v(-372.17, -74.15) * mm, v(-379.99, -87.29) * mm, v(-388.79, -99.78) * mm, v(-398.59, -111.57) * mm, v(-413.02, -126.3) * mm, v(-433.64, -142.67) * mm, v(-462.63, -158.64) * mm, v(-495.97, -170.52) * mm, v(-533.76, -177.94) * mm, v(-562, -179.67) * mm, v(-576.92, -179.67) * mm]});
            skFitSpline(sketch, "E157.trimOffspring", {"points": [v(-576.92, 676.06) * mm, v(-565.9, 676.06) * mm, v(-550.64, 674.2) * mm, v(-532.6, 668.6) * mm, v(-520.2, 663.02) * mm, v(-508.86, 656.21) * mm, v(-498.52, 648.37) * mm, v(-489.1, 639.67) * mm, v(-480.52, 630.28) * mm, v(-473.99, 622.03) * mm, v(-469.1, 615.25) * mm, v(-465.58, 610.1) * mm, v(-462.2, 604.9) * mm, v(-457.87, 597.85) * mm, v(-452.75, 588.87) * mm, v(-447.02, 577.73) * mm, v(-439.88, 562.33) * mm, v(-433.33, 546) * mm, v(-427.13, 528.53) * mm, v(-422.6, 514.8) * mm, v(-418.12, 500.36) * mm, v(-413.63, 485.17) * mm, v(-409.07, 469.16) * mm, v(-404.37, 452.27) * mm, v(-399.58, 434.56) * mm, v(-394.72, 416.12) * mm, v(-389.84, 397.03) * mm, v(-383.36, 370.82) * mm, v(-375.4, 336.85) * mm, v(-366.36, 294.8) * mm, v(-358.15, 252.14) * mm, v(-352.26, 216.62) * mm, v(-348.28, 188.55) * mm, v(-345.7, 167.75) * mm, v(-343.54, 147.28) * mm, v(-341.87, 127.24) * mm, v(-340.72, 107.66) * mm, v(-339.92, 82.18) * mm, v(-340.37, 51.54) * mm, v(-343.54, 16.78) * mm, v(-349.61, -15.88) * mm, v(-357.35, -41.26) * mm, v(-365.3, -60.4) * mm, v(-372.17, -74.15) * mm, v(-379.99, -87.29) * mm, v(-388.79, -99.78) * mm, v(-398.59, -111.57) * mm, v(-413.02, -126.3) * mm, v(-433.64, -142.67) * mm, v(-462.63, -158.64) * mm, v(-495.97, -170.52) * mm, v(-533.76, -177.94) * mm, v(-562, -179.67) * mm, v(-576.92, -179.67) * mm]});
            skFitSpline(sketch, "E158.trimOffspring", {"points": [v(-576.92, 676.06) * mm, v(-565.9, 676.06) * mm, v(-550.64, 674.2) * mm, v(-532.6, 668.6) * mm, v(-520.2, 663.02) * mm, v(-508.86, 656.21) * mm, v(-498.52, 648.37) * mm, v(-489.1, 639.67) * mm, v(-480.52, 630.28) * mm, v(-473.99, 622.03) * mm, v(-469.1, 615.25) * mm, v(-465.58, 610.1) * mm, v(-462.2, 604.9) * mm, v(-457.87, 597.85) * mm, v(-452.75, 588.87) * mm, v(-447.02, 577.73) * mm, v(-439.88, 562.33) * mm, v(-433.33, 546) * mm, v(-427.13, 528.53) * mm, v(-422.6, 514.8) * mm, v(-418.12, 500.36) * mm, v(-413.63, 485.17) * mm, v(-409.07, 469.16) * mm, v(-404.37, 452.27) * mm, v(-399.58, 434.56) * mm, v(-394.72, 416.12) * mm, v(-389.84, 397.03) * mm, v(-383.36, 370.82) * mm, v(-375.4, 336.85) * mm, v(-366.36, 294.8) * mm, v(-358.15, 252.14) * mm, v(-352.26, 216.62) * mm, v(-348.28, 188.55) * mm, v(-345.7, 167.75) * mm, v(-343.54, 147.28) * mm, v(-341.87, 127.24) * mm, v(-340.72, 107.66) * mm, v(-339.92, 82.18) * mm, v(-340.37, 51.54) * mm, v(-343.54, 16.78) * mm, v(-349.61, -15.88) * mm, v(-357.35, -41.26) * mm, v(-365.3, -60.4) * mm, v(-372.17, -74.15) * mm, v(-379.99, -87.29) * mm, v(-388.79, -99.78) * mm, v(-398.59, -111.57) * mm, v(-413.02, -126.3) * mm, v(-433.64, -142.67) * mm, v(-462.63, -158.64) * mm, v(-495.97, -170.52) * mm, v(-533.76, -177.94) * mm, v(-562, -179.67) * mm, v(-576.92, -179.67) * mm]});
            skFitSpline(sketch, "E159.trimOffspring", {"points": [v(-576.92, 676.06) * mm, v(-565.9, 676.06) * mm, v(-550.64, 674.2) * mm, v(-532.6, 668.6) * mm, v(-520.2, 663.02) * mm, v(-508.86, 656.21) * mm, v(-498.52, 648.37) * mm, v(-489.1, 639.67) * mm, v(-480.52, 630.28) * mm, v(-473.99, 622.03) * mm, v(-469.1, 615.25) * mm, v(-465.58, 610.1) * mm, v(-462.2, 604.9) * mm, v(-457.87, 597.85) * mm, v(-452.75, 588.87) * mm, v(-447.02, 577.73) * mm, v(-439.88, 562.33) * mm, v(-433.33, 546) * mm, v(-427.13, 528.53) * mm, v(-422.6, 514.8) * mm, v(-418.12, 500.36) * mm, v(-413.63, 485.17) * mm, v(-409.07, 469.16) * mm, v(-404.37, 452.27) * mm, v(-399.58, 434.56) * mm, v(-394.72, 416.12) * mm, v(-389.84, 397.03) * mm, v(-383.36, 370.82) * mm, v(-375.4, 336.85) * mm, v(-366.36, 294.8) * mm, v(-358.15, 252.14) * mm, v(-352.26, 216.62) * mm, v(-348.28, 188.55) * mm, v(-345.7, 167.75) * mm, v(-343.54, 147.28) * mm, v(-341.87, 127.24) * mm, v(-340.72, 107.66) * mm, v(-339.92, 82.18) * mm, v(-340.37, 51.54) * mm, v(-343.54, 16.78) * mm, v(-349.61, -15.88) * mm, v(-357.35, -41.26) * mm, v(-365.3, -60.4) * mm, v(-372.17, -74.15) * mm, v(-379.99, -87.29) * mm, v(-388.79, -99.78) * mm, v(-398.59, -111.57) * mm, v(-413.02, -126.3) * mm, v(-433.64, -142.67) * mm, v(-462.63, -158.64) * mm, v(-495.97, -170.52) * mm, v(-533.76, -177.94) * mm, v(-562, -179.67) * mm, v(-576.92, -179.67) * mm]});
            skFitSpline(sketch, "E160.trimOffspring", {"points": [v(-576.92, 676.06) * mm, v(-565.9, 676.06) * mm, v(-550.64, 674.2) * mm, v(-532.6, 668.6) * mm, v(-520.2, 663.02) * mm, v(-508.86, 656.21) * mm, v(-498.52, 648.37) * mm, v(-489.1, 639.67) * mm, v(-480.52, 630.28) * mm, v(-473.99, 622.03) * mm, v(-469.1, 615.25) * mm, v(-465.58, 610.1) * mm, v(-462.2, 604.9) * mm, v(-457.87, 597.85) * mm, v(-452.75, 588.87) * mm, v(-447.02, 577.73) * mm, v(-439.88, 562.33) * mm, v(-433.33, 546) * mm, v(-427.13, 528.53) * mm, v(-422.6, 514.8) * mm, v(-418.12, 500.36) * mm, v(-413.63, 485.17) * mm, v(-409.07, 469.16) * mm, v(-404.37, 452.27) * mm, v(-399.58, 434.56) * mm, v(-394.72, 416.12) * mm, v(-389.84, 397.03) * mm, v(-383.36, 370.82) * mm, v(-375.4, 336.85) * mm, v(-366.36, 294.8) * mm, v(-358.15, 252.14) * mm, v(-352.26, 216.62) * mm, v(-348.28, 188.55) * mm, v(-345.7, 167.75) * mm, v(-343.54, 147.28) * mm, v(-341.87, 127.24) * mm, v(-340.72, 107.66) * mm, v(-339.92, 82.18) * mm, v(-340.37, 51.54) * mm, v(-343.54, 16.78) * mm, v(-349.61, -15.88) * mm, v(-357.35, -41.26) * mm, v(-365.3, -60.4) * mm, v(-372.17, -74.15) * mm, v(-379.99, -87.29) * mm, v(-388.79, -99.78) * mm, v(-398.59, -111.57) * mm, v(-413.02, -126.3) * mm, v(-433.64, -142.67) * mm, v(-462.63, -158.64) * mm, v(-495.97, -170.52) * mm, v(-533.76, -177.94) * mm, v(-562, -179.67) * mm, v(-576.92, -179.67) * mm]});
            skLineSegment(sketch, "E161", {"start": v(-576.92, 676.06) * mm, "end": v(-576.92, 670.47) * mm});
            skSolve(sketch);
        }
        {
            var Q0;
            Q0=makeQuery(id+"F2.opExtrude","CAP_FACE",FACE,{"disambiguationData":[OSD([sQuery(id+"F1.wireOp",EDGE,"E54.bottom"),sQuery(id+"F1.wireOp",EDGE,"E54.top"),sQuery(id+"F1.wireOp",EDGE,"E54.left"),sQuery(id+"F1.wireOp",EDGE,"E54.right")])],"isStart":false});
            var sketch = newSketch(context, id + "F4", { "sketchPlane" : qUnion([Q0])});
            skFitSpline(sketch, "E162.0", {"points": [v(-576.92, 666.79) * mm, v(-566.6, 666.79) * mm, v(-547.75, 664.48) * mm, v(-524.04, 655.35) * mm, v(-504.1, 641.7) * mm, v(-490.08, 627.43) * mm, v(-480.14, 614.86) * mm, v(-474.39, 606.64) * mm, v(-470.04, 599.94) * mm, v(-465.85, 593.14) * mm, v(-460.9, 584.46) * mm, v(-455.36, 573.66) * mm, v(-448.4, 558.7) * mm, v(-442, 542.73) * mm, v(-435.9, 525.54) * mm, v(-431.43, 511.98) * mm, v(-427, 497.68) * mm, v(-422.53, 482.59) * mm, v(-418, 466.65) * mm, v(-413.31, 449.82) * mm, v(-408.54, 432.17) * mm, v(-403.7, 413.8) * mm, v(-398.84, 394.77) * mm, v(-392.38, 368.66) * mm, v(-384.44, 334.82) * mm, v(-375.44, 292.95) * mm, v(-367.28, 250.5) * mm, v(-361.43, 215.2) * mm, v(-357.47, 187.32) * mm, v(-354.9, 166.7) * mm, v(-352.77, 146.41) * mm, v(-351.12, 126.58) * mm, v(-349.98, 107.24) * mm, v(-349.19, 82.11) * mm, v(-349.64, 52) * mm, v(-352.74, 18) * mm, v(-358.65, -13.71) * mm, v(-366.12, -38.19) * mm, v(-373.74, -56.55) * mm, v(-380.32, -69.7) * mm, v(-387.78, -82.24) * mm, v(-396.16, -94.14) * mm, v(-405.48, -105.36) * mm, v(-419.19, -119.34) * mm, v(-438.78, -134.9) * mm, v(-466.42, -150.13) * mm, v(-509.04, -165.34) * mm, v(-547.81, -170.4) * mm, v(-576.92, -170.4) * mm]});
            skCircle(sketch, "E163", {"center": v(-553.9, 697.48) * mm, "radius": 4.78 * mm});
            skCircle(sketch, "E164", {"center": v(-453.17, 632.57) * mm, "radius": 4.78 * mm});
            skCircle(sketch, "E165", {"center": v(-403.72, 531.13) * mm, "radius": 4.78 * mm});
            skCircle(sketch, "E166", {"center": v(-374.98, 431.7) * mm, "radius": 4.78 * mm});
            skCircle(sketch, "E167", {"center": v(-350.13, 328.81) * mm, "radius": 4.78 * mm});
            skCircle(sketch, "E168", {"center": v(-330.75, 227.4) * mm, "radius": 4.78 * mm});
            skCircle(sketch, "E169", {"center": v(-318.47, 121.78) * mm, "radius": 4.78 * mm});
            skCircle(sketch, "E170", {"center": v(-321.43, 12.15) * mm, "radius": 4.78 * mm});
            skCircle(sketch, "E171", {"center": v(-358.34, -95.84) * mm, "radius": 4.78 * mm});
            skCircle(sketch, "E172", {"center": v(-444.03, -174.3) * mm, "radius": 4.78 * mm});
            skCircle(sketch, "E173", {"center": v(-553.86, -202.05) * mm, "radius": 4.78 * mm});
            skLineSegment(sketch, "E174", {"start": v(-576.92, 666.79) * mm, "end": v(-615.02, 666.79) * mm});
            skLineSegment(sketch, "E175", {"start": v(-576.92, -170.4) * mm, "end": v(-615.02, -170.4) * mm});
            skLineSegment(sketch, "E176.0", {"start": v(-615.02, 756.2) * mm, "end": v(-615.02, 684.44) * mm});
            skLineSegment(sketch, "E176.1", {"start": v(-615.02, 756.2) * mm, "end": v(-259.42, 756.2) * mm});
            skLineSegment(sketch, "E176.2", {"start": v(-259.42, 756.2) * mm, "end": v(-259.42, -259.8) * mm});
            skLineSegment(sketch, "E176.3", {"start": v(-615.02, -259.8) * mm, "end": v(-259.42, -259.8) * mm});
            skLineSegment(sketch, "E177.trimOffspring", {"start": v(-615.02, -169.34) * mm, "end": v(-615.02, -170.4) * mm, "construction": true});
            skFitSpline(sketch, "E178.0", {"points": [v(-576.92, 682.4) * mm, v(-571.17, 682.4) * mm, v(-560.09, 681.76) * mm, v(-544.64, 679) * mm, v(-530.36, 674.56) * mm, v(-517.25, 668.66) * mm, v(-505.29, 661.48) * mm, v(-494.42, 653.24) * mm, v(-484.58, 644.14) * mm, v(-475.67, 634.4) * mm, v(-468.93, 625.87) * mm, v(-463.9, 618.9) * mm, v(-460.3, 613.62) * mm, v(-456.83, 608.28) * mm, v(-452.4, 601.08) * mm, v(-447.16, 591.89) * mm, v(-441.32, 580.51) * mm, v(-434.03, 564.82) * mm, v(-427.38, 548.25) * mm, v(-421.12, 530.58) * mm, v(-416.55, 516.72) * mm, v(-412.04, 502.2) * mm, v(-407.53, 486.93) * mm, v(-402.95, 470.88) * mm, v(-398.25, 453.95) * mm, v(-393.44, 436.2) * mm, v(-388.58, 417.72) * mm, v(-383.69, 398.58) * mm, v(-377.19, 372.3) * mm, v(-369.2, 338.25) * mm, v(-360.13, 296.08) * mm, v(-351.9, 253.27) * mm, v(-345.99, 217.6) * mm, v(-341.98, 189.4) * mm, v(-339.38, 168.48) * mm, v(-337.22, 147.88) * mm, v(-335.54, 127.7) * mm, v(-334.38, 107.95) * mm, v(-333.56, 82.23) * mm, v(-334.02, 51.23) * mm, v(-337.23, 15.93) * mm, v(-343.43, -17.37) * mm, v(-352.94, -48.56) * mm, v(-363.9, -72.68) * mm, v(-374.66, -90.74) * mm, v(-383.74, -103.64) * mm, v(-393.87, -115.83) * mm, v(-408.79, -131.06) * mm, v(-430.11, -148) * mm, v(-460.04, -164.47) * mm, v(-494.32, -176.68) * mm, v(-533, -184.26) * mm, v(-561.76, -186.02) * mm, v(-576.92, -186.02) * mm]});
            skLineSegment(sketch, "E179.0", {"start": v(-574.6, -230.34) * mm, "end": v(-581.63, -193.22) * mm});
            skFitSpline(sketch, "E179.1", {"points": [v(-576.92, 682.4) * mm, v(-571.17, 682.4) * mm, v(-560.09, 681.76) * mm, v(-544.64, 679) * mm, v(-530.36, 674.56) * mm, v(-517.25, 668.66) * mm, v(-505.29, 661.48) * mm, v(-494.42, 653.24) * mm, v(-484.58, 644.14) * mm, v(-475.67, 634.4) * mm, v(-468.93, 625.87) * mm, v(-463.9, 618.9) * mm, v(-460.3, 613.62) * mm, v(-456.83, 608.28) * mm, v(-452.4, 601.08) * mm, v(-447.16, 591.89) * mm, v(-441.32, 580.51) * mm, v(-434.03, 564.82) * mm, v(-427.38, 548.25) * mm, v(-421.12, 530.58) * mm, v(-416.55, 516.72) * mm, v(-412.04, 502.2) * mm, v(-407.53, 486.93) * mm, v(-402.95, 470.88) * mm, v(-398.25, 453.95) * mm, v(-393.44, 436.2) * mm, v(-388.58, 417.72) * mm, v(-383.69, 398.58) * mm, v(-377.19, 372.3) * mm, v(-369.2, 338.25) * mm, v(-360.13, 296.08) * mm, v(-351.9, 253.27) * mm, v(-345.99, 217.6) * mm, v(-341.98, 189.4) * mm, v(-339.38, 168.48) * mm, v(-337.22, 147.88) * mm, v(-335.54, 127.7) * mm, v(-334.38, 107.95) * mm, v(-333.56, 82.23) * mm, v(-334.02, 51.23) * mm, v(-337.23, 15.93) * mm, v(-343.43, -17.37) * mm, v(-352.94, -48.56) * mm, v(-363.9, -72.68) * mm, v(-374.66, -90.74) * mm, v(-383.74, -103.64) * mm, v(-393.87, -115.83) * mm, v(-408.79, -131.06) * mm, v(-430.11, -148) * mm, v(-460.04, -164.47) * mm, v(-494.32, -176.68) * mm, v(-533, -184.26) * mm, v(-561.76, -186.02) * mm, v(-576.92, -186.02) * mm]});
            skLineSegment(sketch, "E179.2", {"start": v(-346.88, -129) * mm, "end": v(-384.91, -112.09) * mm});
            skLineSegment(sketch, "E179.3", {"start": v(-323.73, -90.17) * mm, "end": v(-346.88, -129) * mm});
            skLineSegment(sketch, "E179.4", {"start": v(-355.56, -65.6) * mm, "end": v(-323.73, -90.17) * mm});
            skLineSegment(sketch, "E179.5", {"start": v(-425.98, -149.88) * mm, "end": v(-411.48, -187.38) * mm});
            skLineSegment(sketch, "E179.6", {"start": v(-411.48, -187.38) * mm, "end": v(-451.4, -208.59) * mm});
            skLineSegment(sketch, "E179.7", {"start": v(-451.4, -208.59) * mm, "end": v(-475.13, -174.5) * mm});
            skFitSpline(sketch, "E179.8", {"points": [v(-576.92, 682.4) * mm, v(-571.17, 682.4) * mm, v(-560.09, 681.76) * mm, v(-544.64, 679) * mm, v(-530.36, 674.56) * mm, v(-517.25, 668.66) * mm, v(-505.29, 661.48) * mm, v(-494.42, 653.24) * mm, v(-484.58, 644.14) * mm, v(-475.67, 634.4) * mm, v(-468.93, 625.87) * mm, v(-463.9, 618.9) * mm, v(-460.3, 613.62) * mm, v(-456.83, 608.28) * mm, v(-452.4, 601.08) * mm, v(-447.16, 591.89) * mm, v(-441.32, 580.51) * mm, v(-434.03, 564.82) * mm, v(-427.38, 548.25) * mm, v(-421.12, 530.58) * mm, v(-416.55, 516.72) * mm, v(-412.04, 502.2) * mm, v(-407.53, 486.93) * mm, v(-402.95, 470.88) * mm, v(-398.25, 453.95) * mm, v(-393.44, 436.2) * mm, v(-388.58, 417.72) * mm, v(-383.69, 398.58) * mm, v(-377.19, 372.3) * mm, v(-369.2, 338.25) * mm, v(-360.13, 296.08) * mm, v(-351.9, 253.27) * mm, v(-345.99, 217.6) * mm, v(-341.98, 189.4) * mm, v(-339.38, 168.48) * mm, v(-337.22, 147.88) * mm, v(-335.54, 127.7) * mm, v(-334.38, 107.95) * mm, v(-333.56, 82.23) * mm, v(-334.02, 51.23) * mm, v(-337.23, 15.93) * mm, v(-343.43, -17.37) * mm, v(-352.94, -48.56) * mm, v(-363.9, -72.68) * mm, v(-374.66, -90.74) * mm, v(-383.74, -103.64) * mm, v(-393.87, -115.83) * mm, v(-408.79, -131.06) * mm, v(-430.11, -148) * mm, v(-460.04, -164.47) * mm, v(-494.32, -176.68) * mm, v(-533, -184.26) * mm, v(-561.76, -186.02) * mm, v(-576.92, -186.02) * mm]});
            skLineSegment(sketch, "E179.9", {"start": v(-527.43, -187.7) * mm, "end": v(-529.5, -227.3) * mm});
            skLineSegment(sketch, "E179.10", {"start": v(-529.5, -227.3) * mm, "end": v(-574.6, -230.34) * mm});
            skLineSegment(sketch, "E180.0", {"start": v(-297.92, -13.88) * mm, "end": v(-337.96, -13.22) * mm});
            skLineSegment(sketch, "E180.1", {"start": v(-291.79, 30.9) * mm, "end": v(-297.92, -13.88) * mm});
            skLineSegment(sketch, "E180.2", {"start": v(-329.97, 40.88) * mm, "end": v(-291.79, 30.9) * mm});
            skFitSpline(sketch, "E180.3", {"points": [v(-576.92, 682.4) * mm, v(-571.17, 682.4) * mm, v(-560.09, 681.76) * mm, v(-544.64, 679) * mm, v(-530.36, 674.56) * mm, v(-517.25, 668.66) * mm, v(-505.29, 661.48) * mm, v(-494.42, 653.24) * mm, v(-484.58, 644.14) * mm, v(-475.67, 634.4) * mm, v(-468.93, 625.87) * mm, v(-463.9, 618.9) * mm, v(-460.3, 613.62) * mm, v(-456.83, 608.28) * mm, v(-452.4, 601.08) * mm, v(-447.16, 591.89) * mm, v(-441.32, 580.51) * mm, v(-434.03, 564.82) * mm, v(-427.38, 548.25) * mm, v(-421.12, 530.58) * mm, v(-416.55, 516.72) * mm, v(-412.04, 502.2) * mm, v(-407.53, 486.93) * mm, v(-402.95, 470.88) * mm, v(-398.25, 453.95) * mm, v(-393.44, 436.2) * mm, v(-388.58, 417.72) * mm, v(-383.69, 398.58) * mm, v(-377.19, 372.3) * mm, v(-369.2, 338.25) * mm, v(-360.13, 296.08) * mm, v(-351.9, 253.27) * mm, v(-345.99, 217.6) * mm, v(-341.98, 189.4) * mm, v(-339.38, 168.48) * mm, v(-337.22, 147.88) * mm, v(-335.54, 127.7) * mm, v(-334.38, 107.95) * mm, v(-333.56, 82.23) * mm, v(-334.02, 51.23) * mm, v(-337.23, 15.93) * mm, v(-343.43, -17.37) * mm, v(-352.94, -48.56) * mm, v(-363.9, -72.68) * mm, v(-374.66, -90.74) * mm, v(-383.74, -103.64) * mm, v(-393.87, -115.83) * mm, v(-408.79, -131.06) * mm, v(-430.11, -148) * mm, v(-460.04, -164.47) * mm, v(-494.32, -176.68) * mm, v(-533, -184.26) * mm, v(-561.76, -186.02) * mm, v(-576.92, -186.02) * mm]});
            skLineSegment(sketch, "E180.4", {"start": v(-290.42, 100.74) * mm, "end": v(-328.61, 93.94) * mm});
            skLineSegment(sketch, "E180.5", {"start": v(-292.97, 145.87) * mm, "end": v(-290.42, 100.74) * mm});
            skLineSegment(sketch, "E180.6", {"start": v(-331.97, 148.33) * mm, "end": v(-292.97, 145.87) * mm});
            skFitSpline(sketch, "E180.7", {"points": [v(-576.92, 682.4) * mm, v(-571.17, 682.4) * mm, v(-560.09, 681.76) * mm, v(-544.64, 679) * mm, v(-530.36, 674.56) * mm, v(-517.25, 668.66) * mm, v(-505.29, 661.48) * mm, v(-494.42, 653.24) * mm, v(-484.58, 644.14) * mm, v(-475.67, 634.4) * mm, v(-468.93, 625.87) * mm, v(-463.9, 618.9) * mm, v(-460.3, 613.62) * mm, v(-456.83, 608.28) * mm, v(-452.4, 601.08) * mm, v(-447.16, 591.89) * mm, v(-441.32, 580.51) * mm, v(-434.03, 564.82) * mm, v(-427.38, 548.25) * mm, v(-421.12, 530.58) * mm, v(-416.55, 516.72) * mm, v(-412.04, 502.2) * mm, v(-407.53, 486.93) * mm, v(-402.95, 470.88) * mm, v(-398.25, 453.95) * mm, v(-393.44, 436.2) * mm, v(-388.58, 417.72) * mm, v(-383.69, 398.58) * mm, v(-377.19, 372.3) * mm, v(-369.2, 338.25) * mm, v(-360.13, 296.08) * mm, v(-351.9, 253.27) * mm, v(-345.99, 217.6) * mm, v(-341.98, 189.4) * mm, v(-339.38, 168.48) * mm, v(-337.22, 147.88) * mm, v(-335.54, 127.7) * mm, v(-334.38, 107.95) * mm, v(-333.56, 82.23) * mm, v(-334.02, 51.23) * mm, v(-337.23, 15.93) * mm, v(-343.43, -17.37) * mm, v(-352.94, -48.56) * mm, v(-363.9, -72.68) * mm, v(-374.66, -90.74) * mm, v(-383.74, -103.64) * mm, v(-393.87, -115.83) * mm, v(-408.79, -131.06) * mm, v(-430.11, -148) * mm, v(-460.04, -164.47) * mm, v(-494.32, -176.68) * mm, v(-533, -184.26) * mm, v(-561.76, -186.02) * mm, v(-576.92, -186.02) * mm]});
            skLineSegment(sketch, "E180.8", {"start": v(-300.76, 209.21) * mm, "end": v(-337.8, 198.77) * mm});
            skLineSegment(sketch, "E180.9", {"start": v(-385.54, 561.13) * mm, "end": v(-371.07, 518.3) * mm});
            skLineSegment(sketch, "E180.10", {"start": v(-423.77, 553.13) * mm, "end": v(-385.54, 561.13) * mm});
            skFitSpline(sketch, "E180.11", {"points": [v(-576.92, 682.4) * mm, v(-571.17, 682.4) * mm, v(-560.09, 681.76) * mm, v(-544.64, 679) * mm, v(-530.36, 674.56) * mm, v(-517.25, 668.66) * mm, v(-505.29, 661.48) * mm, v(-494.42, 653.24) * mm, v(-484.58, 644.14) * mm, v(-475.67, 634.4) * mm, v(-468.93, 625.87) * mm, v(-463.9, 618.9) * mm, v(-460.3, 613.62) * mm, v(-456.83, 608.28) * mm, v(-452.4, 601.08) * mm, v(-447.16, 591.89) * mm, v(-441.32, 580.51) * mm, v(-434.03, 564.82) * mm, v(-427.38, 548.25) * mm, v(-421.12, 530.58) * mm, v(-416.55, 516.72) * mm, v(-412.04, 502.2) * mm, v(-407.53, 486.93) * mm, v(-402.95, 470.88) * mm, v(-398.25, 453.95) * mm, v(-393.44, 436.2) * mm, v(-388.58, 417.72) * mm, v(-383.69, 398.58) * mm, v(-377.19, 372.3) * mm, v(-369.2, 338.25) * mm, v(-360.13, 296.08) * mm, v(-351.9, 253.27) * mm, v(-345.99, 217.6) * mm, v(-341.98, 189.4) * mm, v(-339.38, 168.48) * mm, v(-337.22, 147.88) * mm, v(-335.54, 127.7) * mm, v(-334.38, 107.95) * mm, v(-333.56, 82.23) * mm, v(-334.02, 51.23) * mm, v(-337.23, 15.93) * mm, v(-343.43, -17.37) * mm, v(-352.94, -48.56) * mm, v(-363.9, -72.68) * mm, v(-374.66, -90.74) * mm, v(-383.74, -103.64) * mm, v(-393.87, -115.83) * mm, v(-408.79, -131.06) * mm, v(-430.11, -148) * mm, v(-460.04, -164.47) * mm, v(-494.32, -176.68) * mm, v(-533, -184.26) * mm, v(-561.76, -186.02) * mm, v(-576.92, -186.02) * mm]});
            skLineSegment(sketch, "E180.12", {"start": v(-418.2, 629.9) * mm, "end": v(-447.72, 602.75) * mm});
            skLineSegment(sketch, "E180.13", {"start": v(-444.6, 666.59) * mm, "end": v(-418.2, 629.9) * mm});
            skLineSegment(sketch, "E180.14", {"start": v(-480.88, 646.56) * mm, "end": v(-444.6, 666.59) * mm});
            skLineSegment(sketch, "E180.15", {"start": v(-582.98, 689.05) * mm, "end": v(-572, 727.53) * mm});
            skLineSegment(sketch, "E180.16", {"start": v(-572, 727.53) * mm, "end": v(-527.36, 720.4) * mm});
            skLineSegment(sketch, "E180.17", {"start": v(-527.36, 720.4) * mm, "end": v(-529, 678.2) * mm});
            skFitSpline(sketch, "E180.18", {"points": [v(-576.92, 682.4) * mm, v(-571.17, 682.4) * mm, v(-560.09, 681.76) * mm, v(-544.64, 679) * mm, v(-530.36, 674.56) * mm, v(-517.25, 668.66) * mm, v(-505.29, 661.48) * mm, v(-494.42, 653.24) * mm, v(-484.58, 644.14) * mm, v(-475.67, 634.4) * mm, v(-468.93, 625.87) * mm, v(-463.9, 618.9) * mm, v(-460.3, 613.62) * mm, v(-456.83, 608.28) * mm, v(-452.4, 601.08) * mm, v(-447.16, 591.89) * mm, v(-441.32, 580.51) * mm, v(-434.03, 564.82) * mm, v(-427.38, 548.25) * mm, v(-421.12, 530.58) * mm, v(-416.55, 516.72) * mm, v(-412.04, 502.2) * mm, v(-407.53, 486.93) * mm, v(-402.95, 470.88) * mm, v(-398.25, 453.95) * mm, v(-393.44, 436.2) * mm, v(-388.58, 417.72) * mm, v(-383.69, 398.58) * mm, v(-377.19, 372.3) * mm, v(-369.2, 338.25) * mm, v(-360.13, 296.08) * mm, v(-351.9, 253.27) * mm, v(-345.99, 217.6) * mm, v(-341.98, 189.4) * mm, v(-339.38, 168.48) * mm, v(-337.22, 147.88) * mm, v(-335.54, 127.7) * mm, v(-334.38, 107.95) * mm, v(-333.56, 82.23) * mm, v(-334.02, 51.23) * mm, v(-337.23, 15.93) * mm, v(-343.43, -17.37) * mm, v(-352.94, -48.56) * mm, v(-363.9, -72.68) * mm, v(-374.66, -90.74) * mm, v(-383.74, -103.64) * mm, v(-393.87, -115.83) * mm, v(-408.79, -131.06) * mm, v(-430.11, -148) * mm, v(-460.04, -164.47) * mm, v(-494.32, -176.68) * mm, v(-533, -184.26) * mm, v(-561.76, -186.02) * mm, v(-576.92, -186.02) * mm]});
            skLineSegment(sketch, "E180.19", {"start": v(-371.07, 518.3) * mm, "end": v(-406.26, 501.5) * mm});
            skFitSpline(sketch, "E180.20", {"points": [v(-576.92, 682.4) * mm, v(-571.17, 682.4) * mm, v(-560.09, 681.76) * mm, v(-544.64, 679) * mm, v(-530.36, 674.56) * mm, v(-517.25, 668.66) * mm, v(-505.29, 661.48) * mm, v(-494.42, 653.24) * mm, v(-484.58, 644.14) * mm, v(-475.67, 634.4) * mm, v(-468.93, 625.87) * mm, v(-463.9, 618.9) * mm, v(-460.3, 613.62) * mm, v(-456.83, 608.28) * mm, v(-452.4, 601.08) * mm, v(-447.16, 591.89) * mm, v(-441.32, 580.51) * mm, v(-434.03, 564.82) * mm, v(-427.38, 548.25) * mm, v(-421.12, 530.58) * mm, v(-416.55, 516.72) * mm, v(-412.04, 502.2) * mm, v(-407.53, 486.93) * mm, v(-402.95, 470.88) * mm, v(-398.25, 453.95) * mm, v(-393.44, 436.2) * mm, v(-388.58, 417.72) * mm, v(-383.69, 398.58) * mm, v(-377.19, 372.3) * mm, v(-369.2, 338.25) * mm, v(-360.13, 296.08) * mm, v(-351.9, 253.27) * mm, v(-345.99, 217.6) * mm, v(-341.98, 189.4) * mm, v(-339.38, 168.48) * mm, v(-337.22, 147.88) * mm, v(-335.54, 127.7) * mm, v(-334.38, 107.95) * mm, v(-333.56, 82.23) * mm, v(-334.02, 51.23) * mm, v(-337.23, 15.93) * mm, v(-343.43, -17.37) * mm, v(-352.94, -48.56) * mm, v(-363.9, -72.68) * mm, v(-374.66, -90.74) * mm, v(-383.74, -103.64) * mm, v(-393.87, -115.83) * mm, v(-408.79, -131.06) * mm, v(-430.11, -148) * mm, v(-460.04, -164.47) * mm, v(-494.32, -176.68) * mm, v(-533, -184.26) * mm, v(-561.76, -186.02) * mm, v(-576.92, -186.02) * mm]});
            skLineSegment(sketch, "E180.21", {"start": v(-392.92, 455.18) * mm, "end": v(-354.64, 460.27) * mm});
            skLineSegment(sketch, "E180.22", {"start": v(-354.64, 460.27) * mm, "end": v(-343.37, 416.5) * mm});
            skLineSegment(sketch, "E180.23", {"start": v(-343.37, 416.5) * mm, "end": v(-379, 402.61) * mm});
            skFitSpline(sketch, "E180.24", {"points": [v(-576.92, 682.4) * mm, v(-571.17, 682.4) * mm, v(-560.09, 681.76) * mm, v(-544.64, 679) * mm, v(-530.36, 674.56) * mm, v(-517.25, 668.66) * mm, v(-505.29, 661.48) * mm, v(-494.42, 653.24) * mm, v(-484.58, 644.14) * mm, v(-475.67, 634.4) * mm, v(-468.93, 625.87) * mm, v(-463.9, 618.9) * mm, v(-460.3, 613.62) * mm, v(-456.83, 608.28) * mm, v(-452.4, 601.08) * mm, v(-447.16, 591.89) * mm, v(-441.32, 580.51) * mm, v(-434.03, 564.82) * mm, v(-427.38, 548.25) * mm, v(-421.12, 530.58) * mm, v(-416.55, 516.72) * mm, v(-412.04, 502.2) * mm, v(-407.53, 486.93) * mm, v(-402.95, 470.88) * mm, v(-398.25, 453.95) * mm, v(-393.44, 436.2) * mm, v(-388.58, 417.72) * mm, v(-383.69, 398.58) * mm, v(-377.19, 372.3) * mm, v(-369.2, 338.25) * mm, v(-360.13, 296.08) * mm, v(-351.9, 253.27) * mm, v(-345.99, 217.6) * mm, v(-341.98, 189.4) * mm, v(-339.38, 168.48) * mm, v(-337.22, 147.88) * mm, v(-335.54, 127.7) * mm, v(-334.38, 107.95) * mm, v(-333.56, 82.23) * mm, v(-334.02, 51.23) * mm, v(-337.23, 15.93) * mm, v(-343.43, -17.37) * mm, v(-352.94, -48.56) * mm, v(-363.9, -72.68) * mm, v(-374.66, -90.74) * mm, v(-383.74, -103.64) * mm, v(-393.87, -115.83) * mm, v(-408.79, -131.06) * mm, v(-430.11, -148) * mm, v(-460.04, -164.47) * mm, v(-494.32, -176.68) * mm, v(-533, -184.26) * mm, v(-561.76, -186.02) * mm, v(-576.92, -186.02) * mm]});
            skLineSegment(sketch, "E180.25", {"start": v(-367.02, 352.93) * mm, "end": v(-328.8, 356.66) * mm});
            skLineSegment(sketch, "E180.26", {"start": v(-328.8, 356.66) * mm, "end": v(-319.07, 312.51) * mm});
            skLineSegment(sketch, "E180.27", {"start": v(-319.07, 312.51) * mm, "end": v(-355.45, 299.8) * mm});
            skFitSpline(sketch, "E180.28", {"points": [v(-576.92, 682.4) * mm, v(-571.17, 682.4) * mm, v(-560.09, 681.76) * mm, v(-544.64, 679) * mm, v(-530.36, 674.56) * mm, v(-517.25, 668.66) * mm, v(-505.29, 661.48) * mm, v(-494.42, 653.24) * mm, v(-484.58, 644.14) * mm, v(-475.67, 634.4) * mm, v(-468.93, 625.87) * mm, v(-463.9, 618.9) * mm, v(-460.3, 613.62) * mm, v(-456.83, 608.28) * mm, v(-452.4, 601.08) * mm, v(-447.16, 591.89) * mm, v(-441.32, 580.51) * mm, v(-434.03, 564.82) * mm, v(-427.38, 548.25) * mm, v(-421.12, 530.58) * mm, v(-416.55, 516.72) * mm, v(-412.04, 502.2) * mm, v(-407.53, 486.93) * mm, v(-402.95, 470.88) * mm, v(-398.25, 453.95) * mm, v(-393.44, 436.2) * mm, v(-388.58, 417.72) * mm, v(-383.69, 398.58) * mm, v(-377.19, 372.3) * mm, v(-369.2, 338.25) * mm, v(-360.13, 296.08) * mm, v(-351.9, 253.27) * mm, v(-345.99, 217.6) * mm, v(-341.98, 189.4) * mm, v(-339.38, 168.48) * mm, v(-337.22, 147.88) * mm, v(-335.54, 127.7) * mm, v(-334.38, 107.95) * mm, v(-333.56, 82.23) * mm, v(-334.02, 51.23) * mm, v(-337.23, 15.93) * mm, v(-343.43, -17.37) * mm, v(-352.94, -48.56) * mm, v(-363.9, -72.68) * mm, v(-374.66, -90.74) * mm, v(-383.74, -103.64) * mm, v(-393.87, -115.83) * mm, v(-408.79, -131.06) * mm, v(-430.11, -148) * mm, v(-460.04, -164.47) * mm, v(-494.32, -176.68) * mm, v(-533, -184.26) * mm, v(-561.76, -186.02) * mm, v(-576.92, -186.02) * mm]});
            skLineSegment(sketch, "E180.29", {"start": v(-346.42, 252.5) * mm, "end": v(-307.73, 253.87) * mm});
            skLineSegment(sketch, "E180.30", {"start": v(-307.73, 253.87) * mm, "end": v(-300.76, 209.21) * mm});
            skLineSegment(sketch, "E181", {"start": v(-615.02, -188.05) * mm, "end": v(-587.87, -188.05) * mm});
            skLineSegment(sketch, "E182", {"start": v(-615.02, 684.44) * mm, "end": v(-589.08, 684.44) * mm});
            skLineSegment(sketch, "E183", {"start": v(-615.02, -188.05) * mm, "end": v(-615.02, -259.8) * mm});
            skLineSegment(sketch, "E184", {"start": v(-615.02, 684.44) * mm, "end": v(-615.02, 666.79) * mm});
            skPoint(sketch, "E185.visualSharp", {"position": v(-582.6, -188.05) * mm});
            skArc(sketch, "E185.filletArc", {"start": v(-581.63, -193.22) * mm, "mid": v(-583.81, -189.5) * mm, "end": v(-587.87, -188.05) * mm});
            skPoint(sketch, "E186.visualSharp", {"position": v(-527.17, -182.54) * mm});
            skArc(sketch, "E186.filletArc", {"start": v(-522.12, -181.76) * mm, "mid": v(-525.83, -183.79) * mm, "end": v(-527.43, -187.7) * mm});
            skPoint(sketch, "E187.visualSharp", {"position": v(-477.87, -170.57) * mm});
            skArc(sketch, "E187.filletArc", {"start": v(-475.13, -174.5) * mm, "mid": v(-478.33, -172.1) * mm, "end": v(-482.33, -172.09) * mm});
            skPoint(sketch, "E188.visualSharp", {"position": v(-427.76, -145.27) * mm});
            skArc(sketch, "E188.filletArc", {"start": v(-423.8, -142.46) * mm, "mid": v(-426.15, -145.8) * mm, "end": v(-425.98, -149.88) * mm});
            skPoint(sketch, "E189.visualSharp", {"position": v(-389.24, -110.17) * mm});
            skArc(sketch, "E189.filletArc", {"start": v(-384.91, -112.09) * mm, "mid": v(-388.85, -111.69) * mm, "end": v(-392.26, -113.7) * mm});
            skPoint(sketch, "E190.visualSharp", {"position": v(-359.5, -62.55) * mm});
            skArc(sketch, "E190.filletArc", {"start": v(-357.52, -58.07) * mm, "mid": v(-357.83, -62.16) * mm, "end": v(-355.56, -65.6) * mm});
            skPoint(sketch, "E191.visualSharp", {"position": v(-343.06, -13.14) * mm});
            skArc(sketch, "E191.filletArc", {"start": v(-337.96, -13.22) * mm, "mid": v(-341.94, -14.54) * mm, "end": v(-344.23, -18.05) * mm});
            skPoint(sketch, "E192.visualSharp", {"position": v(-335.04, 42.2) * mm});
            skArc(sketch, "E192.filletArc", {"start": v(-334.7, 47.4) * mm, "mid": v(-333.5, 43.3) * mm, "end": v(-329.97, 40.88) * mm});
            skPoint(sketch, "E193.visualSharp", {"position": v(-333.95, 92.99) * mm});
            skArc(sketch, "E193.filletArc", {"start": v(-328.61, 93.94) * mm, "mid": v(-332.4, 91.73) * mm, "end": v(-333.85, 87.6) * mm});
            skPoint(sketch, "E194.visualSharp", {"position": v(-337.37, 148.67) * mm});
            skArc(sketch, "E194.filletArc", {"start": v(-337.9, 154.03) * mm, "mid": v(-335.98, 150.1) * mm, "end": v(-331.97, 148.33) * mm});
            skPoint(sketch, "E195.visualSharp", {"position": v(-343.12, 197.27) * mm});
            skArc(sketch, "E195.filletArc", {"start": v(-337.8, 198.77) * mm, "mid": v(-341.39, 196.15) * mm, "end": v(-342.37, 191.81) * mm});
            skPoint(sketch, "E196.visualSharp", {"position": v(-351.92, 252.3) * mm});
            skArc(sketch, "E196.filletArc", {"start": v(-352.9, 257.7) * mm, "mid": v(-350.63, 253.9) * mm, "end": v(-346.42, 252.5) * mm});
            skPoint(sketch, "E197.visualSharp", {"position": v(-360.68, 297.96) * mm});
            skArc(sketch, "E197.filletArc", {"start": v(-355.45, 299.8) * mm, "mid": v(-358.87, 296.94) * mm, "end": v(-359.58, 292.54) * mm});
            skPoint(sketch, "E198.visualSharp", {"position": v(-372.56, 352.39) * mm});
            skArc(sketch, "E198.filletArc", {"start": v(-373.82, 357.8) * mm, "mid": v(-371.33, 354.09) * mm, "end": v(-367.02, 352.93) * mm});
            skPoint(sketch, "E199.visualSharp", {"position": v(-384.22, 400.58) * mm});
            skArc(sketch, "E199.filletArc", {"start": v(-379, 402.61) * mm, "mid": v(-382.34, 399.61) * mm, "end": v(-382.85, 395.16) * mm});
            skPoint(sketch, "E200.visualSharp", {"position": v(-398.4, 454.45) * mm});
            skArc(sketch, "E200.filletArc", {"start": v(-399.87, 459.78) * mm, "mid": v(-397.26, 456.17) * mm, "end": v(-392.92, 455.18) * mm});
            skPoint(sketch, "E201.visualSharp", {"position": v(-411.16, 499.17) * mm});
            skArc(sketch, "E201.filletArc", {"start": v(-406.26, 501.5) * mm, "mid": v(-409.33, 498.36) * mm, "end": v(-409.62, 493.98) * mm});
            skPoint(sketch, "E202.visualSharp", {"position": v(-429, 552.04) * mm});
            skArc(sketch, "E202.filletArc", {"start": v(-430.96, 556.97) * mm, "mid": v(-428.06, 553.75) * mm, "end": v(-423.77, 553.13) * mm});
            skPoint(sketch, "E203.visualSharp", {"position": v(-451.44, 599.33) * mm});
            skArc(sketch, "E203.filletArc", {"start": v(-447.72, 602.75) * mm, "mid": v(-449.69, 599.08) * mm, "end": v(-448.97, 594.99) * mm});
            skPoint(sketch, "E204.visualSharp", {"position": v(-485, 644.3) * mm});
            skArc(sketch, "E204.filletArc", {"start": v(-488.3, 647.5) * mm, "mid": v(-484.74, 645.82) * mm, "end": v(-480.88, 646.56) * mm});
            skPoint(sketch, "E205.visualSharp", {"position": v(-529.17, 673.78) * mm});
            skArc(sketch, "E205.filletArc", {"start": v(-529, 678.2) * mm, "mid": v(-528.02, 674.58) * mm, "end": v(-525.18, 672.14) * mm});
            skPoint(sketch, "E206.visualSharp", {"position": v(-584.3, 684.44) * mm});
            skArc(sketch, "E206.filletArc", {"start": v(-589.08, 684.44) * mm, "mid": v(-585.26, 685.72) * mm, "end": v(-582.98, 689.05) * mm});
            skLineSegment(sketch, "E207.0", {"start": v(-576.92, -168.8) * mm, "end": v(-615.02, -168.8) * mm, "construction": true});
            skFitSpline(sketch, "E207.1", {"points": [v(-576.92, 665.2) * mm, v(-566.72, 665.2) * mm, v(-548.12, 662.92) * mm, v(-524.79, 653.94) * mm, v(-508.41, 642.72) * mm, v(-496.82, 632.01) * mm, v(-488.8, 623.26) * mm, v(-481.41, 613.91) * mm, v(-475.7, 605.75) * mm, v(-471.38, 599.09) * mm, v(-467.22, 592.34) * mm, v(-462.3, 583.7) * mm, v(-456.79, 572.96) * mm, v(-449.87, 558.07) * mm, v(-443.49, 542.17) * mm, v(-437.4, 525.03) * mm, v(-432.94, 511.5) * mm, v(-428.51, 497.22) * mm, v(-424.06, 482.15) * mm, v(-419.52, 466.22) * mm, v(-414.84, 449.4) * mm, v(-410.07, 431.76) * mm, v(-405.23, 413.4) * mm, v(-400.38, 394.38) * mm, v(-393.92, 368.29) * mm, v(-385.99, 334.47) * mm, v(-377, 292.64) * mm, v(-368.84, 250.22) * mm, v(-363, 214.95) * mm, v(-359.04, 187.11) * mm, v(-356.48, 166.5) * mm, v(-354.35, 146.26) * mm, v(-352.7, 126.46) * mm, v(-351.57, 107.16) * mm, v(-350.78, 82.1) * mm, v(-351.23, 52.07) * mm, v(-354.31, 18.22) * mm, v(-360.2, -13.34) * mm, v(-367.62, -37.66) * mm, v(-375.19, -55.9) * mm, v(-381.71, -68.95) * mm, v(-389.11, -81.38) * mm, v(-397.42, -93.17) * mm, v(-406.66, -104.3) * mm, v(-420.24, -118.15) * mm, v(-439.66, -133.57) * mm, v(-467.06, -148.68) * mm, v(-498.8, -160) * mm, v(-535.08, -167.13) * mm, v(-562.43, -168.8) * mm, v(-576.92, -168.8) * mm], "construction": true});
            skLineSegment(sketch, "E207.2", {"start": v(-576.92, 665.2) * mm, "end": v(-615.02, 665.2) * mm, "construction": true});
            skLineSegment(sketch, "E208", {"start": v(-615.02, 663.61) * mm, "end": v(-594.78, 663.61) * mm, "construction": true});
            skLineSegment(sketch, "E209.0", {"start": v(-576.92, -169.34) * mm, "end": v(-615.02, -169.34) * mm, "construction": true});
            skFitSpline(sketch, "E209.1", {"points": [v(-576.92, 665.73) * mm, v(-566.68, 665.73) * mm, v(-548, 663.44) * mm, v(-524.54, 654.4) * mm, v(-508.08, 643.14) * mm, v(-496.44, 632.39) * mm, v(-488.4, 623.6) * mm, v(-480.99, 614.23) * mm, v(-475.26, 606.05) * mm, v(-470.93, 599.37) * mm, v(-466.77, 592.6) * mm, v(-461.84, 583.95) * mm, v(-456.31, 573.2) * mm, v(-449.38, 558.27) * mm, v(-443, 542.36) * mm, v(-436.9, 525.2) * mm, v(-432.44, 511.65) * mm, v(-428, 497.37) * mm, v(-423.55, 482.3) * mm, v(-419.01, 466.37) * mm, v(-414.33, 449.54) * mm, v(-409.56, 431.9) * mm, v(-404.72, 413.53) * mm, v(-399.86, 394.51) * mm, v(-393.4, 368.4) * mm, v(-385.47, 334.58) * mm, v(-376.48, 292.74) * mm, v(-368.32, 250.32) * mm, v(-362.47, 215.03) * mm, v(-358.52, 187.18) * mm, v(-355.95, 166.57) * mm, v(-353.83, 146.31) * mm, v(-352.18, 126.5) * mm, v(-351.04, 107.19) * mm, v(-350.25, 82.1) * mm, v(-350.7, 52.05) * mm, v(-353.79, 18.15) * mm, v(-359.68, -13.47) * mm, v(-367.12, -37.84) * mm, v(-374.7, -56.11) * mm, v(-381.25, -69.2) * mm, v(-388.67, -81.66) * mm, v(-397, -93.5) * mm, v(-406.27, -104.65) * mm, v(-419.9, -118.55) * mm, v(-439.37, -134.02) * mm, v(-466.85, -149.16) * mm, v(-498.66, -160.5) * mm, v(-535.02, -167.66) * mm, v(-562.4, -169.34) * mm, v(-576.92, -169.34) * mm], "construction": true});
            skLineSegment(sketch, "E209.2", {"start": v(-576.92, 665.73) * mm, "end": v(-615.02, 665.73) * mm, "construction": true});
            skLineSegment(sketch, "E210", {"start": v(-615.02, 666.79) * mm, "end": v(-615.02, 666.79) * mm});
            skLineSegment(sketch, "E211", {"start": v(-615.02, 666.79) * mm, "end": v(-615.02, 665.73) * mm, "construction": true});
            skLineSegment(sketch, "E212", {"start": v(-615.02, -170.4) * mm, "end": v(-615.02, -170.4) * mm});
            skLineSegment(sketch, "E213", {"start": v(-615.02, -170.4) * mm, "end": v(-615.02, -188.05) * mm});
            skSolve(sketch);
        }
        {
            var Q0;
            Q0=makeQuery(id+"F4.imprint","IMPRINT",FACE,{"disambiguationData":[TD([[makeQuery(id+"F4.imprint","IMPRINT",EDGE,{"derivedFrom":sQuery(id+"F4.wireOp",EDGE,"E162.0")}),1.0]])]});
            extrude(context, id + "F5", {"entities" : qUnion([Q0]), "depth" : 11.76 * mm, "offsetDistance" : 25.4 * mm});
        }
        {
            var Q0;
            {var subQ3=sQuery(id+"F4.wireOp",EDGE,"E176.1");Q0=makeQuery(id+"F4.imprint","IMPRINT",FACE,{"disambiguationData":[TD([[makeQuery(id+"F4.imprint","IMPRINT",EDGE,{"derivedFrom":subQ3}),-1.0]])]});}
            extrude(context, id + "F6", {"entities" : qUnion([Q0]), "operationType" : NewBodyOperationType.ADD, "depth" : 15.44 * mm, "offsetDistance" : 25.4 * mm});
        }
        {
            var Q0;
            Q0=makeQuery(id+"F6.opExtrude","CAP_FACE",FACE,{"disambiguationData":[OSD([sQuery(id+"F4.wireOp",EDGE,"E176.0"),sQuery(id+"F4.wireOp",EDGE,"E176.1"),sQuery(id+"F4.wireOp",EDGE,"E176.2"),sQuery(id+"F4.wireOp",EDGE,"E176.3"),sQuery(id+"F4.wireOp",EDGE,"E177.trimOffspring"),sQuery(id+"F4.wireOp",EDGE,"E178.0"),sQuery(id+"F4.wireOp",EDGE,"E179.0"),sQuery(id+"F4.wireOp",EDGE,"E179.1"),sQuery(id+"F4.wireOp",EDGE,"E179.2"),sQuery(id+"F4.wireOp",EDGE,"E179.3"),sQuery(id+"F4.wireOp",EDGE,"E179.4"),sQuery(id+"F4.wireOp",EDGE,"E179.5"),sQuery(id+"F4.wireOp",EDGE,"E179.6"),sQuery(id+"F4.wireOp",EDGE,"E179.7"),sQuery(id+"F4.wireOp",EDGE,"E179.8"),sQuery(id+"F4.wireOp",EDGE,"E179.9"),sQuery(id+"F4.wireOp",EDGE,"E179.10"),sQuery(id+"F4.wireOp",EDGE,"E180.0"),sQuery(id+"F4.wireOp",EDGE,"E180.1"),sQuery(id+"F4.wireOp",EDGE,"E180.2"),sQuery(id+"F4.wireOp",EDGE,"E180.3"),sQuery(id+"F4.wireOp",EDGE,"E180.4"),sQuery(id+"F4.wireOp",EDGE,"E180.5"),sQuery(id+"F4.wireOp",EDGE,"E180.6"),sQuery(id+"F4.wireOp",EDGE,"E180.7"),sQuery(id+"F4.wireOp",EDGE,"E180.8"),sQuery(id+"F4.wireOp",EDGE,"E180.9"),sQuery(id+"F4.wireOp",EDGE,"E180.10"),sQuery(id+"F4.wireOp",EDGE,"E180.11"),sQuery(id+"F4.wireOp",EDGE,"E180.12"),sQuery(id+"F4.wireOp",EDGE,"E180.13"),sQuery(id+"F4.wireOp",EDGE,"E180.14"),sQuery(id+"F4.wireOp",EDGE,"E180.15"),sQuery(id+"F4.wireOp",EDGE,"E180.16"),sQuery(id+"F4.wireOp",EDGE,"E180.17"),sQuery(id+"F4.wireOp",EDGE,"E180.18"),sQuery(id+"F4.wireOp",EDGE,"E180.19"),sQuery(id+"F4.wireOp",EDGE,"E180.20"),sQuery(id+"F4.wireOp",EDGE,"E180.21"),sQuery(id+"F4.wireOp",EDGE,"E180.22"),sQuery(id+"F4.wireOp",EDGE,"E180.23"),sQuery(id+"F4.wireOp",EDGE,"E180.24"),sQuery(id+"F4.wireOp",EDGE,"E180.25"),sQuery(id+"F4.wireOp",EDGE,"E180.26"),sQuery(id+"F4.wireOp",EDGE,"E180.27"),sQuery(id+"F4.wireOp",EDGE,"E180.28"),sQuery(id+"F4.wireOp",EDGE,"E180.29"),sQuery(id+"F4.wireOp",EDGE,"E180.30"),sQuery(id+"F4.wireOp",EDGE,"E181"),sQuery(id+"F4.wireOp",EDGE,"E182")])],"isStart":false});
            var sketch = newSketch(context, id + "F7", { "sketchPlane" : qUnion([Q0])});
            skArc(sketch, "E214", {"start": v(-553.9, 691.77) * mm, "mid": v(-548.2, 697.48) * mm, "end": v(-553.9, 703.2) * mm});
            skArc(sketch, "E215", {"start": v(-453.17, 626.86) * mm, "mid": v(-447.45, 632.57) * mm, "end": v(-453.17, 638.29) * mm});
            skArc(sketch, "E216", {"start": v(-403.72, 525.42) * mm, "mid": v(-398, 531.13) * mm, "end": v(-403.72, 536.85) * mm});
            skArc(sketch, "E217", {"start": v(-374.98, 425.98) * mm, "mid": v(-369.27, 431.7) * mm, "end": v(-374.98, 437.41) * mm});
            skArc(sketch, "E218", {"start": v(-350.13, 323.1) * mm, "mid": v(-344.41, 328.81) * mm, "end": v(-350.13, 334.53) * mm});
            skArc(sketch, "E219", {"start": v(-330.75, 221.68) * mm, "mid": v(-325.03, 227.4) * mm, "end": v(-330.75, 233.11) * mm});
            skArc(sketch, "E220", {"start": v(-318.47, 116.07) * mm, "mid": v(-312.76, 121.78) * mm, "end": v(-318.47, 127.5) * mm});
            skArc(sketch, "E221", {"start": v(-321.43, 6.43) * mm, "mid": v(-315.72, 12.15) * mm, "end": v(-321.43, 17.86) * mm});
            skArc(sketch, "E222", {"start": v(-358.34, -101.56) * mm, "mid": v(-352.62, -95.84) * mm, "end": v(-358.34, -90.13) * mm});
            skArc(sketch, "E223", {"start": v(-444.03, -180.01) * mm, "mid": v(-438.31, -174.3) * mm, "end": v(-444.03, -168.58) * mm});
            skArc(sketch, "E224", {"start": v(-553.86, -207.77) * mm, "mid": v(-548.14, -202.05) * mm, "end": v(-553.86, -196.34) * mm});
            skFitSpline(sketch, "E225.0", {"points": [v(-576.92, 670.47) * mm, v(-523.93, 670.47) * mm, v(-458.36, 608.09) * mm, v(-410.1, 464.42) * mm, v(-331.77, 140.23) * mm, v(-355.6, -100.03) * mm, v(-480.52, -174.08) * mm, v(-576.92, -174.08) * mm]});
            skLineSegment(sketch, "E226.0", {"start": v(-615.02, 756.2) * mm, "end": v(-615.02, 670.47) * mm});
            skLineSegment(sketch, "E226.1", {"start": v(-615.02, 756.2) * mm, "end": v(-259.42, 756.2) * mm});
            skLineSegment(sketch, "E226.2", {"start": v(-259.42, 756.2) * mm, "end": v(-259.42, -259.8) * mm});
            skLineSegment(sketch, "E226.3", {"start": v(-615.02, -259.8) * mm, "end": v(-259.42, -259.8) * mm});
            skLineSegment(sketch, "E227", {"start": v(-576.92, 670.47) * mm, "end": v(-615.02, 670.47) * mm});
            skLineSegment(sketch, "E228", {"start": v(-576.92, -174.08) * mm, "end": v(-615.02, -174.08) * mm});
            skLineSegment(sketch, "E229.trimOffspring", {"start": v(-615.02, -174.08) * mm, "end": v(-615.02, -259.8) * mm});
            skLineSegment(sketch, "E230.0", {"start": v(-576.92, -172.5) * mm, "end": v(-615.02, -172.5) * mm});
            skFitSpline(sketch, "E230.1", {"points": [v(-576.92, 668.88) * mm, v(-566.44, 668.88) * mm, v(-547.25, 666.54) * mm, v(-523.05, 657.22) * mm, v(-502.74, 643.3) * mm, v(-488.5, 628.82) * mm, v(-478.45, 616.1) * mm, v(-471.5, 606.16) * mm, v(-465.05, 595.96) * mm, v(-457.07, 581.95) * mm, v(-448.09, 563.52) * mm, v(-440.04, 543.47) * mm, v(-433.92, 526.22) * mm, v(-429.43, 512.61) * mm, v(-424.98, 498.28) * mm, v(-420.52, 483.17) * mm, v(-415.97, 467.22) * mm, v(-411.3, 450.37) * mm, v(-406.51, 432.7) * mm, v(-401.67, 414.32) * mm, v(-396.8, 395.28) * mm, v(-390.34, 369.15) * mm, v(-382.4, 335.28) * mm, v(-373.39, 293.37) * mm, v(-365.21, 250.87) * mm, v(-359.36, 215.52) * mm, v(-355.4, 187.6) * mm, v(-352.82, 166.93) * mm, v(-350.69, 146.6) * mm, v(-349.03, 126.73) * mm, v(-347.89, 107.33) * mm, v(-347.1, 82.13) * mm, v(-347.54, 51.9) * mm, v(-350.66, 17.73) * mm, v(-356.6, -14.2) * mm, v(-364.14, -38.88) * mm, v(-371.83, -57.42) * mm, v(-378.48, -70.71) * mm, v(-386.02, -83.38) * mm, v(-394.5, -95.41) * mm, v(-403.92, -106.76) * mm, v(-417.8, -120.91) * mm, v(-437.62, -136.66) * mm, v(-465.56, -152.06) * mm, v(-508.6, -167.4) * mm, v(-547.65, -172.5) * mm, v(-576.92, -172.5) * mm]});
            skLineSegment(sketch, "E230.2", {"start": v(-576.92, 668.88) * mm, "end": v(-615.02, 668.88) * mm});
            skLineSegment(sketch, "E231", {"start": v(-553.9, 703.2) * mm, "end": v(-569.15, 703.2) * mm});
            skArc(sketch, "E232", {"start": v(-569.15, 703.2) * mm, "mid": v(-574.86, 697.48) * mm, "end": v(-569.15, 691.77) * mm});
            skLineSegment(sketch, "E233", {"start": v(-553.9, 691.77) * mm, "end": v(-569.15, 691.77) * mm});
            skLineSegment(sketch, "E234", {"start": v(-453.17, 638.29) * mm, "end": v(-468.4, 638.29) * mm});
            skArc(sketch, "E235", {"start": v(-468.4, 638.29) * mm, "mid": v(-474.12, 632.57) * mm, "end": v(-468.4, 626.86) * mm});
            skLineSegment(sketch, "E236", {"start": v(-453.17, 626.86) * mm, "end": v(-468.4, 626.86) * mm});
            skLineSegment(sketch, "E237", {"start": v(-403.72, 536.85) * mm, "end": v(-418.96, 536.85) * mm});
            skArc(sketch, "E238", {"start": v(-418.96, 536.85) * mm, "mid": v(-424.67, 531.13) * mm, "end": v(-418.96, 525.42) * mm});
            skLineSegment(sketch, "E239", {"start": v(-403.72, 525.42) * mm, "end": v(-418.96, 525.42) * mm});
            skLineSegment(sketch, "E240", {"start": v(-374.98, 437.41) * mm, "end": v(-390.22, 437.41) * mm});
            skArc(sketch, "E241", {"start": v(-390.22, 437.41) * mm, "mid": v(-395.94, 431.7) * mm, "end": v(-390.22, 425.98) * mm});
            skLineSegment(sketch, "E242", {"start": v(-374.98, 425.98) * mm, "end": v(-390.22, 425.98) * mm});
            skLineSegment(sketch, "E243", {"start": v(-350.13, 334.53) * mm, "end": v(-365.37, 334.53) * mm});
            skArc(sketch, "E244", {"start": v(-365.37, 334.53) * mm, "mid": v(-371.08, 328.81) * mm, "end": v(-365.37, 323.1) * mm});
            skLineSegment(sketch, "E245", {"start": v(-350.13, 323.1) * mm, "end": v(-365.37, 323.1) * mm});
            skLineSegment(sketch, "E246", {"start": v(-330.75, 233.11) * mm, "end": v(-345.99, 233.11) * mm});
            skArc(sketch, "E247", {"start": v(-345.99, 233.11) * mm, "mid": v(-351.7, 227.4) * mm, "end": v(-345.99, 221.68) * mm});
            skLineSegment(sketch, "E248", {"start": v(-330.75, 221.68) * mm, "end": v(-345.99, 221.68) * mm});
            skLineSegment(sketch, "E249", {"start": v(-318.47, 127.5) * mm, "end": v(-333.71, 127.5) * mm});
            skArc(sketch, "E250", {"start": v(-333.71, 127.5) * mm, "mid": v(-339.43, 121.78) * mm, "end": v(-333.71, 116.07) * mm});
            skLineSegment(sketch, "E251", {"start": v(-318.47, 116.07) * mm, "end": v(-333.71, 116.07) * mm});
            skLineSegment(sketch, "E252", {"start": v(-321.43, 17.86) * mm, "end": v(-336.67, 17.86) * mm});
            skArc(sketch, "E253", {"start": v(-336.67, 17.86) * mm, "mid": v(-342.39, 12.15) * mm, "end": v(-336.67, 6.43) * mm});
            skLineSegment(sketch, "E254", {"start": v(-321.43, 6.43) * mm, "end": v(-336.67, 6.43) * mm});
            skLineSegment(sketch, "E255", {"start": v(-358.34, -90.13) * mm, "end": v(-373.58, -90.13) * mm});
            skArc(sketch, "E256", {"start": v(-373.58, -90.13) * mm, "mid": v(-379.3, -95.84) * mm, "end": v(-373.58, -101.56) * mm});
            skLineSegment(sketch, "E257", {"start": v(-358.34, -101.56) * mm, "end": v(-373.58, -101.56) * mm});
            skLineSegment(sketch, "E258", {"start": v(-444.03, -168.58) * mm, "end": v(-459.27, -168.58) * mm});
            skArc(sketch, "E259", {"start": v(-459.27, -168.58) * mm, "mid": v(-464.98, -174.3) * mm, "end": v(-459.27, -180.01) * mm});
            skLineSegment(sketch, "E260", {"start": v(-444.03, -180.01) * mm, "end": v(-459.27, -180.01) * mm});
            skLineSegment(sketch, "E261", {"start": v(-553.86, -196.34) * mm, "end": v(-569.1, -196.34) * mm});
            skArc(sketch, "E262", {"start": v(-569.1, -196.34) * mm, "mid": v(-574.81, -202.05) * mm, "end": v(-569.1, -207.77) * mm});
            skLineSegment(sketch, "E263", {"start": v(-553.86, -207.77) * mm, "end": v(-569.1, -207.77) * mm});
            skSolve(sketch);
        }
        {
            var Q0;
            Q0 = qSketchRegion(id + "F7", true);
            extrude(context, id + "F8", {"entities" : qUnion([Q0]), "depth" : 15.44 * mm, "offsetDistance" : 25.4 * mm});
        }
        {
            var Q0;
            Q0=makeQuery(id+"F2.opExtrude","CAP_FACE",FACE,{"disambiguationData":[OSD([sQuery(id+"F1.wireOp",EDGE,"E54.bottom"),sQuery(id+"F1.wireOp",EDGE,"E54.top"),sQuery(id+"F1.wireOp",EDGE,"E54.left"),sQuery(id+"F1.wireOp",EDGE,"E54.right")])],"isStart":false});
            var sketch = newSketch(context, id + "F9", { "sketchPlane" : qUnion([Q0])});
            skFitSpline(sketch, "E264.0", {"points": [v(-576.92, 666.79) * mm, v(-566.6, 666.79) * mm, v(-547.75, 664.48) * mm, v(-524.04, 655.35) * mm, v(-504.1, 641.7) * mm, v(-490.08, 627.43) * mm, v(-480.14, 614.86) * mm, v(-474.39, 606.64) * mm, v(-470.04, 599.94) * mm, v(-465.85, 593.14) * mm, v(-460.9, 584.46) * mm, v(-455.36, 573.66) * mm, v(-448.4, 558.7) * mm, v(-442, 542.73) * mm, v(-435.9, 525.54) * mm, v(-431.43, 511.98) * mm, v(-427, 497.68) * mm, v(-422.53, 482.59) * mm, v(-418, 466.65) * mm, v(-413.31, 449.82) * mm, v(-408.54, 432.17) * mm, v(-403.7, 413.8) * mm, v(-398.84, 394.77) * mm, v(-392.38, 368.66) * mm, v(-384.44, 334.82) * mm, v(-375.44, 292.95) * mm, v(-367.28, 250.5) * mm, v(-361.43, 215.2) * mm, v(-357.47, 187.32) * mm, v(-354.9, 166.7) * mm, v(-352.77, 146.41) * mm, v(-351.12, 126.58) * mm, v(-349.98, 107.24) * mm, v(-349.19, 82.11) * mm, v(-349.64, 52) * mm, v(-352.74, 18) * mm, v(-358.65, -13.71) * mm, v(-366.12, -38.19) * mm, v(-373.74, -56.55) * mm, v(-380.32, -69.7) * mm, v(-387.78, -82.24) * mm, v(-396.16, -94.14) * mm, v(-405.48, -105.36) * mm, v(-419.19, -119.34) * mm, v(-438.78, -134.9) * mm, v(-466.42, -150.13) * mm, v(-509.04, -165.34) * mm, v(-547.81, -170.4) * mm, v(-576.92, -170.4) * mm]});
            skLineSegment(sketch, "E265.0", {"start": v(-615.02, 666.79) * mm, "end": v(-615.02, -170.4) * mm});
            skLineSegment(sketch, "E266", {"start": v(-576.92, 666.79) * mm, "end": v(-615.02, 666.79) * mm});
            skLineSegment(sketch, "E267", {"start": v(-576.92, -170.4) * mm, "end": v(-615.02, -170.4) * mm});
            skPoint(sketch, "E268.orphan", {"position": v(-615.02, 756.2) * mm});
            skPoint(sketch, "E269.orphan", {"position": v(-615.02, -259.8) * mm});
            skSolve(sketch);
        }
        {
            var Q0;
            Q0=makeQuery(id+"F9.imprint","IMPRINT",FACE,{"disambiguationData":[TD([[makeQuery(id+"F9.imprint","IMPRINT",EDGE,{"derivedFrom":sQuery(id+"F9.wireOp",EDGE,"E264.0")}),-1.0]])]});
            extrude(context, id + "F10", {"entities" : qUnion([Q0]), "operationType" : NewBodyOperationType.ADD, "depth" : 36.02 * mm, "offsetDistance" : 25.4 * mm});
        }
    });
